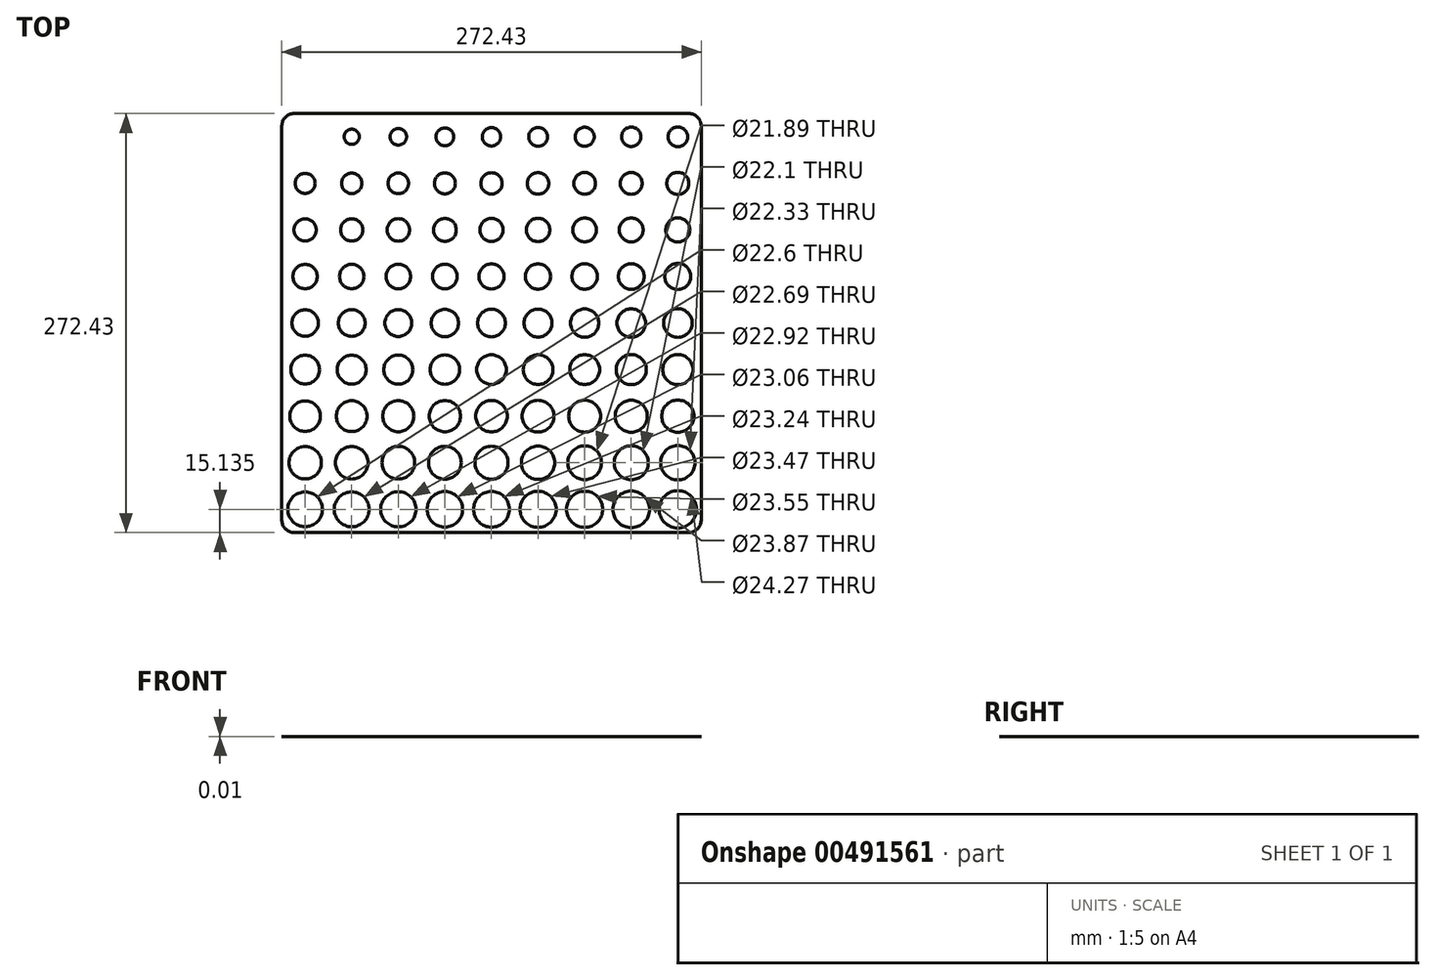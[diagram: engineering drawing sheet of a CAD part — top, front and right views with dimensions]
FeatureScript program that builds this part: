
annotation { "Feature Type Name" : "Feature", "Feature Type Description" : "" }
export const myFeature = defineFeature(function(context is Context, id is Id, definition is map)
    precondition{}
    {
        {
            var Q0;
            Q0=qCreatedBy(makeId("Top.planeOp"),FACE);
            var sketch = newSketch(context, id + "F0", { "sketchPlane" : qUnion([Q0])});
            skLineSegment(sketch, "E0.bottom", {"start": v(0, 0) * mm, "end": v(30.27, 0) * mm, "construction": true});
            skLineSegment(sketch, "E0.top", {"start": v(0, -30.27) * mm, "end": v(30.27, -30.27) * mm, "construction": true});
            skLineSegment(sketch, "E0.left", {"start": v(0, 0) * mm, "end": v(0, -30.27) * mm, "construction": true});
            skLineSegment(sketch, "E0.right", {"start": v(30.27, 0) * mm, "end": v(30.27, -30.27) * mm, "construction": true});
            skLineSegment(sketch, "E1", {"start": v(0, -15.13) * mm, "end": v(30.27, -15.13) * mm, "construction": true});
            skLineSegment(sketch, "E2", {"start": v(15.14, 0) * mm, "end": v(15.14, -30.27) * mm, "construction": true});
            skPoint(sketch, "E3", {"position": v(15.14, -15.14) * mm});
            skLineSegment(sketch, "E4.0.1.0", {"start": v(0, -30.27) * mm, "end": v(0, -60.54) * mm, "construction": true});
            skLineSegment(sketch, "E4.0.1.1", {"start": v(15.14, -30.27) * mm, "end": v(15.14, -60.54) * mm, "construction": true});
            skLineSegment(sketch, "E4.0.1.2", {"start": v(30.27, -30.27) * mm, "end": v(30.27, -60.54) * mm, "construction": true});
            skLineSegment(sketch, "E4.0.1.4", {"start": v(0, -60.54) * mm, "end": v(30.27, -60.54) * mm, "construction": true});
            skPoint(sketch, "E4.0.1.5", {"position": v(15.14, -45.4) * mm});
            skLineSegment(sketch, "E4.0.2.0", {"start": v(0, -60.54) * mm, "end": v(0, -90.81) * mm, "construction": true});
            skLineSegment(sketch, "E4.0.2.1", {"start": v(15.14, -60.54) * mm, "end": v(15.14, -90.81) * mm, "construction": true});
            skLineSegment(sketch, "E4.0.2.2", {"start": v(30.27, -60.54) * mm, "end": v(30.27, -90.81) * mm, "construction": true});
            skLineSegment(sketch, "E4.0.2.3", {"start": v(0, -60.54) * mm, "end": v(30.27, -60.54) * mm, "construction": true});
            skLineSegment(sketch, "E4.0.2.4", {"start": v(0, -90.81) * mm, "end": v(30.27, -90.81) * mm, "construction": true});
            skPoint(sketch, "E4.0.2.5", {"position": v(15.14, -75.68) * mm});
            skLineSegment(sketch, "E4.0.3.0", {"start": v(0, -90.81) * mm, "end": v(0, -121.08) * mm, "construction": true});
            skLineSegment(sketch, "E4.0.3.1", {"start": v(15.14, -90.81) * mm, "end": v(15.14, -121.08) * mm, "construction": true});
            skLineSegment(sketch, "E4.0.3.2", {"start": v(30.27, -90.81) * mm, "end": v(30.27, -121.08) * mm, "construction": true});
            skLineSegment(sketch, "E4.0.3.3", {"start": v(0, -90.81) * mm, "end": v(30.27, -90.81) * mm, "construction": true});
            skLineSegment(sketch, "E4.0.3.4", {"start": v(0, -121.08) * mm, "end": v(30.27, -121.08) * mm, "construction": true});
            skPoint(sketch, "E4.0.3.5", {"position": v(15.14, -105.94) * mm});
            skLineSegment(sketch, "E4.0.4.0", {"start": v(0, -121.08) * mm, "end": v(0, -151.35) * mm, "construction": true});
            skLineSegment(sketch, "E4.0.4.1", {"start": v(15.14, -121.08) * mm, "end": v(15.14, -151.35) * mm, "construction": true});
            skLineSegment(sketch, "E4.0.4.2", {"start": v(30.27, -121.08) * mm, "end": v(30.27, -151.35) * mm, "construction": true});
            skLineSegment(sketch, "E4.0.4.3", {"start": v(0, -121.08) * mm, "end": v(30.27, -121.08) * mm, "construction": true});
            skLineSegment(sketch, "E4.0.4.4", {"start": v(0, -151.35) * mm, "end": v(30.27, -151.35) * mm, "construction": true});
            skPoint(sketch, "E4.0.4.5", {"position": v(15.14, -136.22) * mm});
            skLineSegment(sketch, "E4.0.5.0", {"start": v(0, -151.35) * mm, "end": v(0, -181.62) * mm, "construction": true});
            skLineSegment(sketch, "E4.0.5.1", {"start": v(15.14, -151.35) * mm, "end": v(15.14, -181.62) * mm, "construction": true});
            skLineSegment(sketch, "E4.0.5.2", {"start": v(30.27, -151.35) * mm, "end": v(30.27, -181.62) * mm, "construction": true});
            skLineSegment(sketch, "E4.0.5.3", {"start": v(0, -151.35) * mm, "end": v(30.27, -151.35) * mm, "construction": true});
            skLineSegment(sketch, "E4.0.5.4", {"start": v(0, -181.62) * mm, "end": v(30.27, -181.62) * mm, "construction": true});
            skPoint(sketch, "E4.0.5.5", {"position": v(15.14, -166.49) * mm});
            skLineSegment(sketch, "E4.0.6.0", {"start": v(0, -181.62) * mm, "end": v(0, -211.89) * mm, "construction": true});
            skLineSegment(sketch, "E4.0.6.1", {"start": v(15.14, -181.62) * mm, "end": v(15.14, -211.9) * mm, "construction": true});
            skLineSegment(sketch, "E4.0.6.2", {"start": v(30.27, -181.62) * mm, "end": v(30.27, -211.89) * mm, "construction": true});
            skLineSegment(sketch, "E4.0.6.3", {"start": v(0, -181.62) * mm, "end": v(30.27, -181.62) * mm, "construction": true});
            skLineSegment(sketch, "E4.0.6.4", {"start": v(0, -211.89) * mm, "end": v(30.27, -211.89) * mm, "construction": true});
            skPoint(sketch, "E4.0.6.5", {"position": v(15.14, -196.76) * mm});
            skLineSegment(sketch, "E4.0.7.0", {"start": v(0, -211.9) * mm, "end": v(0, -242.16) * mm, "construction": true});
            skLineSegment(sketch, "E4.0.7.1", {"start": v(15.14, -211.9) * mm, "end": v(15.14, -242.16) * mm, "construction": true});
            skLineSegment(sketch, "E4.0.7.2", {"start": v(30.27, -211.9) * mm, "end": v(30.27, -242.16) * mm, "construction": true});
            skLineSegment(sketch, "E4.0.7.3", {"start": v(0, -211.9) * mm, "end": v(30.27, -211.9) * mm, "construction": true});
            skLineSegment(sketch, "E4.0.7.4", {"start": v(0, -242.16) * mm, "end": v(30.27, -242.16) * mm, "construction": true});
            skPoint(sketch, "E4.0.7.5", {"position": v(15.14, -227.03) * mm});
            skLineSegment(sketch, "E4.0.8.0", {"start": v(0, -242.16) * mm, "end": v(0, -272.43) * mm, "construction": true});
            skLineSegment(sketch, "E4.0.8.1", {"start": v(15.14, -242.16) * mm, "end": v(15.14, -272.43) * mm, "construction": true});
            skLineSegment(sketch, "E4.0.8.2", {"start": v(30.27, -242.16) * mm, "end": v(30.27, -272.43) * mm, "construction": true});
            skLineSegment(sketch, "E4.0.8.3", {"start": v(0, -242.16) * mm, "end": v(30.27, -242.16) * mm, "construction": true});
            skLineSegment(sketch, "E4.0.8.4", {"start": v(0, -272.43) * mm, "end": v(30.27, -272.43) * mm, "construction": true});
            skPoint(sketch, "E4.0.8.5", {"position": v(15.14, -257.3) * mm});
            skLineSegment(sketch, "E4.1.0.1", {"start": v(45.4, 0) * mm, "end": v(45.4, -30.27) * mm, "construction": true});
            skLineSegment(sketch, "E4.1.0.2", {"start": v(60.54, 0) * mm, "end": v(60.54, -30.27) * mm, "construction": true});
            skLineSegment(sketch, "E4.1.0.3", {"start": v(30.27, 0) * mm, "end": v(60.54, 0) * mm, "construction": true});
            skLineSegment(sketch, "E4.1.0.4", {"start": v(30.27, -30.27) * mm, "end": v(60.54, -30.27) * mm, "construction": true});
            skPoint(sketch, "E4.1.0.5", {"position": v(45.4, -15.14) * mm});
            skLineSegment(sketch, "E4.1.1.0", {"start": v(30.27, -30.27) * mm, "end": v(30.27, -60.54) * mm, "construction": true});
            skLineSegment(sketch, "E4.1.1.1", {"start": v(45.4, -30.27) * mm, "end": v(45.4, -60.54) * mm, "construction": true});
            skLineSegment(sketch, "E4.1.1.2", {"start": v(60.54, -30.27) * mm, "end": v(60.54, -60.54) * mm, "construction": true});
            skLineSegment(sketch, "E4.1.1.3", {"start": v(30.27, -30.27) * mm, "end": v(60.54, -30.27) * mm, "construction": true});
            skLineSegment(sketch, "E4.1.1.4", {"start": v(30.27, -60.54) * mm, "end": v(60.54, -60.54) * mm, "construction": true});
            skPoint(sketch, "E4.1.1.5", {"position": v(45.4, -45.4) * mm});
            skLineSegment(sketch, "E4.1.2.0", {"start": v(30.27, -60.54) * mm, "end": v(30.27, -90.81) * mm, "construction": true});
            skLineSegment(sketch, "E4.1.2.1", {"start": v(45.4, -60.54) * mm, "end": v(45.4, -90.81) * mm, "construction": true});
            skLineSegment(sketch, "E4.1.2.2", {"start": v(60.54, -60.54) * mm, "end": v(60.54, -90.81) * mm, "construction": true});
            skLineSegment(sketch, "E4.1.2.3", {"start": v(30.27, -60.54) * mm, "end": v(60.54, -60.54) * mm, "construction": true});
            skLineSegment(sketch, "E4.1.2.4", {"start": v(30.27, -90.81) * mm, "end": v(60.54, -90.81) * mm, "construction": true});
            skPoint(sketch, "E4.1.2.5", {"position": v(45.4, -75.68) * mm});
            skLineSegment(sketch, "E4.1.3.0", {"start": v(30.27, -90.81) * mm, "end": v(30.27, -121.08) * mm, "construction": true});
            skLineSegment(sketch, "E4.1.3.1", {"start": v(45.4, -90.81) * mm, "end": v(45.4, -121.08) * mm, "construction": true});
            skLineSegment(sketch, "E4.1.3.2", {"start": v(60.54, -90.81) * mm, "end": v(60.54, -121.08) * mm, "construction": true});
            skLineSegment(sketch, "E4.1.3.3", {"start": v(30.27, -90.81) * mm, "end": v(60.54, -90.81) * mm, "construction": true});
            skLineSegment(sketch, "E4.1.3.4", {"start": v(30.27, -121.08) * mm, "end": v(60.54, -121.08) * mm, "construction": true});
            skPoint(sketch, "E4.1.3.5", {"position": v(45.4, -105.94) * mm});
            skLineSegment(sketch, "E4.1.4.0", {"start": v(30.27, -121.08) * mm, "end": v(30.27, -151.35) * mm, "construction": true});
            skLineSegment(sketch, "E4.1.4.1", {"start": v(45.4, -121.08) * mm, "end": v(45.4, -151.35) * mm, "construction": true});
            skLineSegment(sketch, "E4.1.4.2", {"start": v(60.54, -121.08) * mm, "end": v(60.54, -151.35) * mm, "construction": true});
            skLineSegment(sketch, "E4.1.4.3", {"start": v(30.27, -121.08) * mm, "end": v(60.54, -121.08) * mm, "construction": true});
            skLineSegment(sketch, "E4.1.4.4", {"start": v(30.27, -151.35) * mm, "end": v(60.54, -151.35) * mm, "construction": true});
            skPoint(sketch, "E4.1.4.5", {"position": v(45.4, -136.22) * mm});
            skLineSegment(sketch, "E4.1.5.0", {"start": v(30.27, -151.35) * mm, "end": v(30.27, -181.62) * mm, "construction": true});
            skLineSegment(sketch, "E4.1.5.1", {"start": v(45.4, -151.35) * mm, "end": v(45.4, -181.62) * mm, "construction": true});
            skLineSegment(sketch, "E4.1.5.2", {"start": v(60.54, -151.35) * mm, "end": v(60.54, -181.62) * mm, "construction": true});
            skLineSegment(sketch, "E4.1.5.3", {"start": v(30.27, -151.35) * mm, "end": v(60.54, -151.35) * mm, "construction": true});
            skLineSegment(sketch, "E4.1.5.4", {"start": v(30.27, -181.62) * mm, "end": v(60.54, -181.62) * mm, "construction": true});
            skPoint(sketch, "E4.1.5.5", {"position": v(45.4, -166.49) * mm});
            skLineSegment(sketch, "E4.1.6.0", {"start": v(30.27, -181.62) * mm, "end": v(30.27, -211.89) * mm, "construction": true});
            skLineSegment(sketch, "E4.1.6.1", {"start": v(45.4, -181.62) * mm, "end": v(45.4, -211.9) * mm, "construction": true});
            skLineSegment(sketch, "E4.1.6.2", {"start": v(60.54, -181.62) * mm, "end": v(60.54, -211.89) * mm, "construction": true});
            skLineSegment(sketch, "E4.1.6.3", {"start": v(30.27, -181.62) * mm, "end": v(60.54, -181.62) * mm, "construction": true});
            skLineSegment(sketch, "E4.1.6.4", {"start": v(30.27, -211.89) * mm, "end": v(60.54, -211.89) * mm, "construction": true});
            skPoint(sketch, "E4.1.6.5", {"position": v(45.4, -196.76) * mm});
            skLineSegment(sketch, "E4.1.7.0", {"start": v(30.27, -211.9) * mm, "end": v(30.27, -242.16) * mm, "construction": true});
            skLineSegment(sketch, "E4.1.7.1", {"start": v(45.4, -211.9) * mm, "end": v(45.4, -242.16) * mm, "construction": true});
            skLineSegment(sketch, "E4.1.7.2", {"start": v(60.54, -211.9) * mm, "end": v(60.54, -242.16) * mm, "construction": true});
            skLineSegment(sketch, "E4.1.7.3", {"start": v(30.27, -211.9) * mm, "end": v(60.54, -211.9) * mm, "construction": true});
            skLineSegment(sketch, "E4.1.7.4", {"start": v(30.27, -242.16) * mm, "end": v(60.54, -242.16) * mm, "construction": true});
            skPoint(sketch, "E4.1.7.5", {"position": v(45.4, -227.03) * mm});
            skLineSegment(sketch, "E4.1.8.0", {"start": v(30.27, -242.16) * mm, "end": v(30.27, -272.43) * mm, "construction": true});
            skLineSegment(sketch, "E4.1.8.1", {"start": v(45.4, -242.16) * mm, "end": v(45.4, -272.43) * mm, "construction": true});
            skLineSegment(sketch, "E4.1.8.2", {"start": v(60.54, -242.16) * mm, "end": v(60.54, -272.43) * mm, "construction": true});
            skLineSegment(sketch, "E4.1.8.3", {"start": v(30.27, -242.16) * mm, "end": v(60.54, -242.16) * mm, "construction": true});
            skLineSegment(sketch, "E4.1.8.4", {"start": v(30.27, -272.43) * mm, "end": v(60.54, -272.43) * mm, "construction": true});
            skPoint(sketch, "E4.1.8.5", {"position": v(45.4, -257.3) * mm});
            skLineSegment(sketch, "E4.2.0.0", {"start": v(60.54, 0) * mm, "end": v(60.54, -30.27) * mm, "construction": true});
            skLineSegment(sketch, "E4.2.0.1", {"start": v(75.68, 0) * mm, "end": v(75.68, -30.27) * mm, "construction": true});
            skLineSegment(sketch, "E4.2.0.2", {"start": v(90.81, 0) * mm, "end": v(90.81, -30.27) * mm, "construction": true});
            skLineSegment(sketch, "E4.2.0.3", {"start": v(60.54, 0) * mm, "end": v(90.81, 0) * mm, "construction": true});
            skLineSegment(sketch, "E4.2.0.4", {"start": v(60.54, -30.27) * mm, "end": v(90.81, -30.27) * mm, "construction": true});
            skPoint(sketch, "E4.2.0.5", {"position": v(75.68, -15.14) * mm});
            skLineSegment(sketch, "E4.2.1.0", {"start": v(60.54, -30.27) * mm, "end": v(60.54, -60.54) * mm, "construction": true});
            skLineSegment(sketch, "E4.2.1.1", {"start": v(75.68, -30.27) * mm, "end": v(75.68, -60.54) * mm, "construction": true});
            skLineSegment(sketch, "E4.2.1.2", {"start": v(90.81, -30.27) * mm, "end": v(90.81, -60.54) * mm, "construction": true});
            skLineSegment(sketch, "E4.2.1.3", {"start": v(60.54, -30.27) * mm, "end": v(90.81, -30.27) * mm, "construction": true});
            skLineSegment(sketch, "E4.2.1.4", {"start": v(60.54, -60.54) * mm, "end": v(90.81, -60.54) * mm, "construction": true});
            skPoint(sketch, "E4.2.1.5", {"position": v(75.68, -45.4) * mm});
            skLineSegment(sketch, "E4.2.2.0", {"start": v(60.54, -60.54) * mm, "end": v(60.54, -90.81) * mm, "construction": true});
            skLineSegment(sketch, "E4.2.2.1", {"start": v(75.68, -60.54) * mm, "end": v(75.68, -90.81) * mm, "construction": true});
            skLineSegment(sketch, "E4.2.2.2", {"start": v(90.81, -60.54) * mm, "end": v(90.81, -90.81) * mm, "construction": true});
            skLineSegment(sketch, "E4.2.2.3", {"start": v(60.54, -60.54) * mm, "end": v(90.81, -60.54) * mm, "construction": true});
            skLineSegment(sketch, "E4.2.2.4", {"start": v(60.54, -90.81) * mm, "end": v(90.81, -90.81) * mm, "construction": true});
            skPoint(sketch, "E4.2.2.5", {"position": v(75.68, -75.68) * mm});
            skLineSegment(sketch, "E4.2.3.0", {"start": v(60.54, -90.81) * mm, "end": v(60.54, -121.08) * mm, "construction": true});
            skLineSegment(sketch, "E4.2.3.1", {"start": v(75.68, -90.81) * mm, "end": v(75.68, -121.08) * mm, "construction": true});
            skLineSegment(sketch, "E4.2.3.2", {"start": v(90.81, -90.81) * mm, "end": v(90.81, -121.08) * mm, "construction": true});
            skLineSegment(sketch, "E4.2.3.3", {"start": v(60.54, -90.81) * mm, "end": v(90.81, -90.81) * mm, "construction": true});
            skLineSegment(sketch, "E4.2.3.4", {"start": v(60.54, -121.08) * mm, "end": v(90.81, -121.08) * mm, "construction": true});
            skPoint(sketch, "E4.2.3.5", {"position": v(75.68, -105.94) * mm});
            skLineSegment(sketch, "E4.2.4.0", {"start": v(60.54, -121.08) * mm, "end": v(60.54, -151.35) * mm, "construction": true});
            skLineSegment(sketch, "E4.2.4.1", {"start": v(75.68, -121.08) * mm, "end": v(75.68, -151.35) * mm, "construction": true});
            skLineSegment(sketch, "E4.2.4.2", {"start": v(90.81, -121.08) * mm, "end": v(90.81, -151.35) * mm, "construction": true});
            skLineSegment(sketch, "E4.2.4.3", {"start": v(60.54, -121.08) * mm, "end": v(90.81, -121.08) * mm, "construction": true});
            skLineSegment(sketch, "E4.2.4.4", {"start": v(60.54, -151.35) * mm, "end": v(90.81, -151.35) * mm, "construction": true});
            skPoint(sketch, "E4.2.4.5", {"position": v(75.68, -136.22) * mm});
            skLineSegment(sketch, "E4.2.5.0", {"start": v(60.54, -151.35) * mm, "end": v(60.54, -181.62) * mm, "construction": true});
            skLineSegment(sketch, "E4.2.5.1", {"start": v(75.68, -151.35) * mm, "end": v(75.68, -181.62) * mm, "construction": true});
            skLineSegment(sketch, "E4.2.5.2", {"start": v(90.81, -151.35) * mm, "end": v(90.81, -181.62) * mm, "construction": true});
            skLineSegment(sketch, "E4.2.5.3", {"start": v(60.54, -151.35) * mm, "end": v(90.81, -151.35) * mm, "construction": true});
            skLineSegment(sketch, "E4.2.5.4", {"start": v(60.54, -181.62) * mm, "end": v(90.81, -181.62) * mm, "construction": true});
            skPoint(sketch, "E4.2.5.5", {"position": v(75.68, -166.49) * mm});
            skLineSegment(sketch, "E4.2.6.0", {"start": v(60.54, -181.62) * mm, "end": v(60.54, -211.89) * mm, "construction": true});
            skLineSegment(sketch, "E4.2.6.1", {"start": v(75.68, -181.62) * mm, "end": v(75.68, -211.9) * mm, "construction": true});
            skLineSegment(sketch, "E4.2.6.2", {"start": v(90.81, -181.62) * mm, "end": v(90.81, -211.89) * mm, "construction": true});
            skLineSegment(sketch, "E4.2.6.3", {"start": v(60.54, -181.62) * mm, "end": v(90.81, -181.62) * mm, "construction": true});
            skLineSegment(sketch, "E4.2.6.4", {"start": v(60.54, -211.89) * mm, "end": v(90.81, -211.89) * mm, "construction": true});
            skPoint(sketch, "E4.2.6.5", {"position": v(75.68, -196.76) * mm});
            skLineSegment(sketch, "E4.2.7.0", {"start": v(60.54, -211.9) * mm, "end": v(60.54, -242.16) * mm, "construction": true});
            skLineSegment(sketch, "E4.2.7.1", {"start": v(75.68, -211.9) * mm, "end": v(75.68, -242.16) * mm, "construction": true});
            skLineSegment(sketch, "E4.2.7.2", {"start": v(90.81, -211.9) * mm, "end": v(90.81, -242.16) * mm, "construction": true});
            skLineSegment(sketch, "E4.2.7.3", {"start": v(60.54, -211.9) * mm, "end": v(90.81, -211.9) * mm, "construction": true});
            skLineSegment(sketch, "E4.2.7.4", {"start": v(60.54, -242.16) * mm, "end": v(90.81, -242.16) * mm, "construction": true});
            skPoint(sketch, "E4.2.7.5", {"position": v(75.68, -227.03) * mm});
            skLineSegment(sketch, "E4.2.8.0", {"start": v(60.54, -242.16) * mm, "end": v(60.54, -272.43) * mm, "construction": true});
            skLineSegment(sketch, "E4.2.8.1", {"start": v(75.68, -242.16) * mm, "end": v(75.68, -272.43) * mm, "construction": true});
            skLineSegment(sketch, "E4.2.8.2", {"start": v(90.81, -242.16) * mm, "end": v(90.81, -272.43) * mm, "construction": true});
            skLineSegment(sketch, "E4.2.8.3", {"start": v(60.54, -242.16) * mm, "end": v(90.81, -242.16) * mm, "construction": true});
            skLineSegment(sketch, "E4.2.8.4", {"start": v(60.54, -272.43) * mm, "end": v(90.81, -272.43) * mm, "construction": true});
            skPoint(sketch, "E4.2.8.5", {"position": v(75.68, -257.3) * mm});
            skLineSegment(sketch, "E4.3.0.0", {"start": v(90.81, 0) * mm, "end": v(90.81, -30.27) * mm, "construction": true});
            skLineSegment(sketch, "E4.3.0.1", {"start": v(105.95, 0) * mm, "end": v(105.95, -30.27) * mm, "construction": true});
            skLineSegment(sketch, "E4.3.0.2", {"start": v(121.08, 0) * mm, "end": v(121.08, -30.27) * mm, "construction": true});
            skLineSegment(sketch, "E4.3.0.3", {"start": v(90.81, 0) * mm, "end": v(121.08, 0) * mm, "construction": true});
            skLineSegment(sketch, "E4.3.0.4", {"start": v(90.81, -30.27) * mm, "end": v(121.08, -30.27) * mm, "construction": true});
            skPoint(sketch, "E4.3.0.5", {"position": v(105.95, -15.14) * mm});
            skLineSegment(sketch, "E4.3.1.0", {"start": v(90.81, -30.27) * mm, "end": v(90.81, -60.54) * mm, "construction": true});
            skLineSegment(sketch, "E4.3.1.1", {"start": v(105.95, -30.27) * mm, "end": v(105.95, -60.54) * mm, "construction": true});
            skLineSegment(sketch, "E4.3.1.2", {"start": v(121.08, -30.27) * mm, "end": v(121.08, -60.54) * mm, "construction": true});
            skLineSegment(sketch, "E4.3.1.3", {"start": v(90.81, -30.27) * mm, "end": v(121.08, -30.27) * mm, "construction": true});
            skLineSegment(sketch, "E4.3.1.4", {"start": v(90.81, -60.54) * mm, "end": v(121.08, -60.54) * mm, "construction": true});
            skPoint(sketch, "E4.3.1.5", {"position": v(105.95, -45.4) * mm});
            skLineSegment(sketch, "E4.3.2.0", {"start": v(90.81, -60.54) * mm, "end": v(90.81, -90.81) * mm, "construction": true});
            skLineSegment(sketch, "E4.3.2.1", {"start": v(105.95, -60.54) * mm, "end": v(105.95, -90.81) * mm, "construction": true});
            skLineSegment(sketch, "E4.3.2.2", {"start": v(121.08, -60.54) * mm, "end": v(121.08, -90.81) * mm, "construction": true});
            skLineSegment(sketch, "E4.3.2.3", {"start": v(90.81, -60.54) * mm, "end": v(121.08, -60.54) * mm, "construction": true});
            skLineSegment(sketch, "E4.3.2.4", {"start": v(90.81, -90.81) * mm, "end": v(121.08, -90.81) * mm, "construction": true});
            skPoint(sketch, "E4.3.2.5", {"position": v(105.95, -75.68) * mm});
            skLineSegment(sketch, "E4.3.3.0", {"start": v(90.81, -90.81) * mm, "end": v(90.81, -121.08) * mm, "construction": true});
            skLineSegment(sketch, "E4.3.3.1", {"start": v(105.95, -90.81) * mm, "end": v(105.95, -121.08) * mm, "construction": true});
            skLineSegment(sketch, "E4.3.3.2", {"start": v(121.08, -90.81) * mm, "end": v(121.08, -121.08) * mm, "construction": true});
            skLineSegment(sketch, "E4.3.3.3", {"start": v(90.81, -90.81) * mm, "end": v(121.08, -90.81) * mm, "construction": true});
            skLineSegment(sketch, "E4.3.3.4", {"start": v(90.81, -121.08) * mm, "end": v(121.08, -121.08) * mm, "construction": true});
            skPoint(sketch, "E4.3.3.5", {"position": v(105.95, -105.94) * mm});
            skLineSegment(sketch, "E4.3.4.0", {"start": v(90.81, -121.08) * mm, "end": v(90.81, -151.35) * mm, "construction": true});
            skLineSegment(sketch, "E4.3.4.1", {"start": v(105.95, -121.08) * mm, "end": v(105.95, -151.35) * mm, "construction": true});
            skLineSegment(sketch, "E4.3.4.2", {"start": v(121.08, -121.08) * mm, "end": v(121.08, -151.35) * mm, "construction": true});
            skLineSegment(sketch, "E4.3.4.3", {"start": v(90.81, -121.08) * mm, "end": v(121.08, -121.08) * mm, "construction": true});
            skLineSegment(sketch, "E4.3.4.4", {"start": v(90.81, -151.35) * mm, "end": v(121.08, -151.35) * mm, "construction": true});
            skPoint(sketch, "E4.3.4.5", {"position": v(105.95, -136.22) * mm});
            skLineSegment(sketch, "E4.3.5.0", {"start": v(90.81, -151.35) * mm, "end": v(90.81, -181.62) * mm, "construction": true});
            skLineSegment(sketch, "E4.3.5.1", {"start": v(105.95, -151.35) * mm, "end": v(105.95, -181.62) * mm, "construction": true});
            skLineSegment(sketch, "E4.3.5.2", {"start": v(121.08, -151.35) * mm, "end": v(121.08, -181.62) * mm, "construction": true});
            skLineSegment(sketch, "E4.3.5.3", {"start": v(90.81, -151.35) * mm, "end": v(121.08, -151.35) * mm, "construction": true});
            skLineSegment(sketch, "E4.3.5.4", {"start": v(90.81, -181.62) * mm, "end": v(121.08, -181.62) * mm, "construction": true});
            skPoint(sketch, "E4.3.5.5", {"position": v(105.95, -166.49) * mm});
            skLineSegment(sketch, "E4.3.6.0", {"start": v(90.81, -181.62) * mm, "end": v(90.81, -211.89) * mm, "construction": true});
            skLineSegment(sketch, "E4.3.6.1", {"start": v(105.95, -181.62) * mm, "end": v(105.95, -211.9) * mm, "construction": true});
            skLineSegment(sketch, "E4.3.6.2", {"start": v(121.08, -181.62) * mm, "end": v(121.08, -211.89) * mm, "construction": true});
            skLineSegment(sketch, "E4.3.6.3", {"start": v(90.81, -181.62) * mm, "end": v(121.08, -181.62) * mm, "construction": true});
            skLineSegment(sketch, "E4.3.6.4", {"start": v(90.81, -211.89) * mm, "end": v(121.08, -211.89) * mm, "construction": true});
            skPoint(sketch, "E4.3.6.5", {"position": v(105.95, -196.76) * mm});
            skLineSegment(sketch, "E4.3.7.0", {"start": v(90.81, -211.9) * mm, "end": v(90.81, -242.16) * mm, "construction": true});
            skLineSegment(sketch, "E4.3.7.1", {"start": v(105.95, -211.9) * mm, "end": v(105.95, -242.16) * mm, "construction": true});
            skLineSegment(sketch, "E4.3.7.2", {"start": v(121.08, -211.9) * mm, "end": v(121.08, -242.16) * mm, "construction": true});
            skLineSegment(sketch, "E4.3.7.3", {"start": v(90.81, -211.9) * mm, "end": v(121.08, -211.9) * mm, "construction": true});
            skLineSegment(sketch, "E4.3.7.4", {"start": v(90.81, -242.16) * mm, "end": v(121.08, -242.16) * mm, "construction": true});
            skPoint(sketch, "E4.3.7.5", {"position": v(105.95, -227.03) * mm});
            skLineSegment(sketch, "E4.3.8.0", {"start": v(90.81, -242.16) * mm, "end": v(90.81, -272.43) * mm, "construction": true});
            skLineSegment(sketch, "E4.3.8.1", {"start": v(105.95, -242.16) * mm, "end": v(105.95, -272.43) * mm, "construction": true});
            skLineSegment(sketch, "E4.3.8.2", {"start": v(121.08, -242.16) * mm, "end": v(121.08, -272.43) * mm, "construction": true});
            skLineSegment(sketch, "E4.3.8.3", {"start": v(90.81, -242.16) * mm, "end": v(121.08, -242.16) * mm, "construction": true});
            skLineSegment(sketch, "E4.3.8.4", {"start": v(90.81, -272.43) * mm, "end": v(121.08, -272.43) * mm, "construction": true});
            skPoint(sketch, "E4.3.8.5", {"position": v(105.95, -257.3) * mm});
            skLineSegment(sketch, "E4.4.0.0", {"start": v(121.08, 0) * mm, "end": v(121.08, -30.27) * mm, "construction": true});
            skLineSegment(sketch, "E4.4.0.1", {"start": v(136.22, 0) * mm, "end": v(136.22, -30.27) * mm, "construction": true});
            skLineSegment(sketch, "E4.4.0.2", {"start": v(151.35, 0) * mm, "end": v(151.35, -30.27) * mm, "construction": true});
            skLineSegment(sketch, "E4.4.0.3", {"start": v(121.08, 0) * mm, "end": v(151.35, 0) * mm, "construction": true});
            skLineSegment(sketch, "E4.4.0.4", {"start": v(121.08, -30.27) * mm, "end": v(151.35, -30.27) * mm, "construction": true});
            skPoint(sketch, "E4.4.0.5", {"position": v(136.22, -15.14) * mm});
            skLineSegment(sketch, "E4.4.1.0", {"start": v(121.08, -30.27) * mm, "end": v(121.08, -60.54) * mm, "construction": true});
            skLineSegment(sketch, "E4.4.1.1", {"start": v(136.22, -30.27) * mm, "end": v(136.22, -60.54) * mm, "construction": true});
            skLineSegment(sketch, "E4.4.1.2", {"start": v(151.35, -30.27) * mm, "end": v(151.35, -60.54) * mm, "construction": true});
            skLineSegment(sketch, "E4.4.1.3", {"start": v(121.08, -30.27) * mm, "end": v(151.35, -30.27) * mm, "construction": true});
            skLineSegment(sketch, "E4.4.1.4", {"start": v(121.08, -60.54) * mm, "end": v(151.35, -60.54) * mm, "construction": true});
            skPoint(sketch, "E4.4.1.5", {"position": v(136.22, -45.4) * mm});
            skLineSegment(sketch, "E4.4.2.0", {"start": v(121.08, -60.54) * mm, "end": v(121.08, -90.81) * mm, "construction": true});
            skLineSegment(sketch, "E4.4.2.1", {"start": v(136.22, -60.54) * mm, "end": v(136.22, -90.81) * mm, "construction": true});
            skLineSegment(sketch, "E4.4.2.2", {"start": v(151.35, -60.54) * mm, "end": v(151.35, -90.81) * mm, "construction": true});
            skLineSegment(sketch, "E4.4.2.3", {"start": v(121.08, -60.54) * mm, "end": v(151.35, -60.54) * mm, "construction": true});
            skLineSegment(sketch, "E4.4.2.4", {"start": v(121.08, -90.81) * mm, "end": v(151.35, -90.81) * mm, "construction": true});
            skPoint(sketch, "E4.4.2.5", {"position": v(136.22, -75.68) * mm});
            skLineSegment(sketch, "E4.4.3.0", {"start": v(121.08, -90.81) * mm, "end": v(121.08, -121.08) * mm, "construction": true});
            skLineSegment(sketch, "E4.4.3.1", {"start": v(136.22, -90.81) * mm, "end": v(136.22, -121.08) * mm, "construction": true});
            skLineSegment(sketch, "E4.4.3.2", {"start": v(151.35, -90.81) * mm, "end": v(151.35, -121.08) * mm, "construction": true});
            skLineSegment(sketch, "E4.4.3.3", {"start": v(121.08, -90.81) * mm, "end": v(151.35, -90.81) * mm, "construction": true});
            skLineSegment(sketch, "E4.4.3.4", {"start": v(121.08, -121.08) * mm, "end": v(151.35, -121.08) * mm, "construction": true});
            skPoint(sketch, "E4.4.3.5", {"position": v(136.22, -105.94) * mm});
            skLineSegment(sketch, "E4.4.4.0", {"start": v(121.08, -121.08) * mm, "end": v(121.08, -151.35) * mm, "construction": true});
            skLineSegment(sketch, "E4.4.4.1", {"start": v(136.22, -121.08) * mm, "end": v(136.22, -151.35) * mm, "construction": true});
            skLineSegment(sketch, "E4.4.4.2", {"start": v(151.35, -121.08) * mm, "end": v(151.35, -151.35) * mm, "construction": true});
            skLineSegment(sketch, "E4.4.4.3", {"start": v(121.08, -121.08) * mm, "end": v(151.35, -121.08) * mm, "construction": true});
            skLineSegment(sketch, "E4.4.4.4", {"start": v(121.08, -151.35) * mm, "end": v(151.35, -151.35) * mm, "construction": true});
            skPoint(sketch, "E4.4.4.5", {"position": v(136.22, -136.22) * mm});
            skLineSegment(sketch, "E4.4.5.0", {"start": v(121.08, -151.35) * mm, "end": v(121.08, -181.62) * mm, "construction": true});
            skLineSegment(sketch, "E4.4.5.1", {"start": v(136.22, -151.35) * mm, "end": v(136.22, -181.62) * mm, "construction": true});
            skLineSegment(sketch, "E4.4.5.2", {"start": v(151.35, -151.35) * mm, "end": v(151.35, -181.62) * mm, "construction": true});
            skLineSegment(sketch, "E4.4.5.3", {"start": v(121.08, -151.35) * mm, "end": v(151.35, -151.35) * mm, "construction": true});
            skLineSegment(sketch, "E4.4.5.4", {"start": v(121.08, -181.62) * mm, "end": v(151.35, -181.62) * mm, "construction": true});
            skPoint(sketch, "E4.4.5.5", {"position": v(136.22, -166.49) * mm});
            skLineSegment(sketch, "E4.4.6.0", {"start": v(121.08, -181.62) * mm, "end": v(121.08, -211.89) * mm, "construction": true});
            skLineSegment(sketch, "E4.4.6.1", {"start": v(136.22, -181.62) * mm, "end": v(136.22, -211.9) * mm, "construction": true});
            skLineSegment(sketch, "E4.4.6.2", {"start": v(151.35, -181.62) * mm, "end": v(151.35, -211.89) * mm, "construction": true});
            skLineSegment(sketch, "E4.4.6.3", {"start": v(121.08, -181.62) * mm, "end": v(151.35, -181.62) * mm, "construction": true});
            skLineSegment(sketch, "E4.4.6.4", {"start": v(121.08, -211.89) * mm, "end": v(151.35, -211.89) * mm, "construction": true});
            skPoint(sketch, "E4.4.6.5", {"position": v(136.22, -196.76) * mm});
            skLineSegment(sketch, "E4.4.7.0", {"start": v(121.08, -211.9) * mm, "end": v(121.08, -242.16) * mm, "construction": true});
            skLineSegment(sketch, "E4.4.7.1", {"start": v(136.22, -211.9) * mm, "end": v(136.22, -242.16) * mm, "construction": true});
            skLineSegment(sketch, "E4.4.7.2", {"start": v(151.35, -211.9) * mm, "end": v(151.35, -242.16) * mm, "construction": true});
            skLineSegment(sketch, "E4.4.7.3", {"start": v(121.08, -211.9) * mm, "end": v(151.35, -211.9) * mm, "construction": true});
            skLineSegment(sketch, "E4.4.7.4", {"start": v(121.08, -242.16) * mm, "end": v(151.35, -242.16) * mm, "construction": true});
            skPoint(sketch, "E4.4.7.5", {"position": v(136.22, -227.03) * mm});
            skLineSegment(sketch, "E4.4.8.0", {"start": v(121.08, -242.16) * mm, "end": v(121.08, -272.43) * mm, "construction": true});
            skLineSegment(sketch, "E4.4.8.1", {"start": v(136.22, -242.16) * mm, "end": v(136.22, -272.43) * mm, "construction": true});
            skLineSegment(sketch, "E4.4.8.2", {"start": v(151.35, -242.16) * mm, "end": v(151.35, -272.43) * mm, "construction": true});
            skLineSegment(sketch, "E4.4.8.3", {"start": v(121.08, -242.16) * mm, "end": v(151.35, -242.16) * mm, "construction": true});
            skLineSegment(sketch, "E4.4.8.4", {"start": v(121.08, -272.43) * mm, "end": v(151.35, -272.43) * mm, "construction": true});
            skPoint(sketch, "E4.4.8.5", {"position": v(136.22, -257.3) * mm});
            skLineSegment(sketch, "E4.5.0.0", {"start": v(151.35, 0) * mm, "end": v(151.35, -30.27) * mm, "construction": true});
            skLineSegment(sketch, "E4.5.0.1", {"start": v(166.49, 0) * mm, "end": v(166.49, -30.27) * mm, "construction": true});
            skLineSegment(sketch, "E4.5.0.2", {"start": v(181.62, 0) * mm, "end": v(181.62, -30.27) * mm, "construction": true});
            skLineSegment(sketch, "E4.5.0.3", {"start": v(151.35, 0) * mm, "end": v(181.62, 0) * mm, "construction": true});
            skLineSegment(sketch, "E4.5.0.4", {"start": v(151.35, -30.27) * mm, "end": v(181.62, -30.27) * mm, "construction": true});
            skPoint(sketch, "E4.5.0.5", {"position": v(166.49, -15.14) * mm});
            skLineSegment(sketch, "E4.5.1.0", {"start": v(151.35, -30.27) * mm, "end": v(151.35, -60.54) * mm, "construction": true});
            skLineSegment(sketch, "E4.5.1.1", {"start": v(166.49, -30.27) * mm, "end": v(166.49, -60.54) * mm, "construction": true});
            skLineSegment(sketch, "E4.5.1.2", {"start": v(181.62, -30.27) * mm, "end": v(181.62, -60.54) * mm, "construction": true});
            skLineSegment(sketch, "E4.5.1.3", {"start": v(151.35, -30.27) * mm, "end": v(181.62, -30.27) * mm, "construction": true});
            skLineSegment(sketch, "E4.5.1.4", {"start": v(151.35, -60.54) * mm, "end": v(181.62, -60.54) * mm, "construction": true});
            skPoint(sketch, "E4.5.1.5", {"position": v(166.49, -45.4) * mm});
            skLineSegment(sketch, "E4.5.2.0", {"start": v(151.35, -60.54) * mm, "end": v(151.35, -90.81) * mm, "construction": true});
            skLineSegment(sketch, "E4.5.2.1", {"start": v(166.49, -60.54) * mm, "end": v(166.49, -90.81) * mm, "construction": true});
            skLineSegment(sketch, "E4.5.2.2", {"start": v(181.62, -60.54) * mm, "end": v(181.62, -90.81) * mm, "construction": true});
            skLineSegment(sketch, "E4.5.2.3", {"start": v(151.35, -60.54) * mm, "end": v(181.62, -60.54) * mm, "construction": true});
            skLineSegment(sketch, "E4.5.2.4", {"start": v(151.35, -90.81) * mm, "end": v(181.62, -90.81) * mm, "construction": true});
            skPoint(sketch, "E4.5.2.5", {"position": v(166.49, -75.68) * mm});
            skLineSegment(sketch, "E4.5.3.0", {"start": v(151.35, -90.81) * mm, "end": v(151.35, -121.08) * mm, "construction": true});
            skLineSegment(sketch, "E4.5.3.1", {"start": v(166.49, -90.81) * mm, "end": v(166.49, -121.08) * mm, "construction": true});
            skLineSegment(sketch, "E4.5.3.2", {"start": v(181.62, -90.81) * mm, "end": v(181.62, -121.08) * mm, "construction": true});
            skLineSegment(sketch, "E4.5.3.3", {"start": v(151.35, -90.81) * mm, "end": v(181.62, -90.81) * mm, "construction": true});
            skLineSegment(sketch, "E4.5.3.4", {"start": v(151.35, -121.08) * mm, "end": v(181.62, -121.08) * mm, "construction": true});
            skPoint(sketch, "E4.5.3.5", {"position": v(166.49, -105.94) * mm});
            skLineSegment(sketch, "E4.5.4.0", {"start": v(151.35, -121.08) * mm, "end": v(151.35, -151.35) * mm, "construction": true});
            skLineSegment(sketch, "E4.5.4.1", {"start": v(166.49, -121.08) * mm, "end": v(166.49, -151.35) * mm, "construction": true});
            skLineSegment(sketch, "E4.5.4.2", {"start": v(181.62, -121.08) * mm, "end": v(181.62, -151.35) * mm, "construction": true});
            skLineSegment(sketch, "E4.5.4.3", {"start": v(151.35, -121.08) * mm, "end": v(181.62, -121.08) * mm, "construction": true});
            skLineSegment(sketch, "E4.5.4.4", {"start": v(151.35, -151.35) * mm, "end": v(181.62, -151.35) * mm, "construction": true});
            skPoint(sketch, "E4.5.4.5", {"position": v(166.49, -136.22) * mm});
            skLineSegment(sketch, "E4.5.5.0", {"start": v(151.35, -151.35) * mm, "end": v(151.35, -181.62) * mm, "construction": true});
            skLineSegment(sketch, "E4.5.5.1", {"start": v(166.49, -151.35) * mm, "end": v(166.49, -181.62) * mm, "construction": true});
            skLineSegment(sketch, "E4.5.5.2", {"start": v(181.62, -151.35) * mm, "end": v(181.62, -181.62) * mm, "construction": true});
            skLineSegment(sketch, "E4.5.5.3", {"start": v(151.35, -151.35) * mm, "end": v(181.62, -151.35) * mm, "construction": true});
            skLineSegment(sketch, "E4.5.5.4", {"start": v(151.35, -181.62) * mm, "end": v(181.62, -181.62) * mm, "construction": true});
            skPoint(sketch, "E4.5.5.5", {"position": v(166.49, -166.49) * mm});
            skLineSegment(sketch, "E4.5.6.0", {"start": v(151.35, -181.62) * mm, "end": v(151.35, -211.89) * mm, "construction": true});
            skLineSegment(sketch, "E4.5.6.1", {"start": v(166.49, -181.62) * mm, "end": v(166.49, -211.9) * mm, "construction": true});
            skLineSegment(sketch, "E4.5.6.2", {"start": v(181.62, -181.62) * mm, "end": v(181.62, -211.89) * mm, "construction": true});
            skLineSegment(sketch, "E4.5.6.3", {"start": v(151.35, -181.62) * mm, "end": v(181.62, -181.62) * mm, "construction": true});
            skLineSegment(sketch, "E4.5.6.4", {"start": v(151.35, -211.89) * mm, "end": v(181.62, -211.89) * mm, "construction": true});
            skPoint(sketch, "E4.5.6.5", {"position": v(166.49, -196.76) * mm});
            skLineSegment(sketch, "E4.5.7.0", {"start": v(151.35, -211.9) * mm, "end": v(151.35, -242.16) * mm, "construction": true});
            skLineSegment(sketch, "E4.5.7.1", {"start": v(166.49, -211.9) * mm, "end": v(166.49, -242.16) * mm, "construction": true});
            skLineSegment(sketch, "E4.5.7.2", {"start": v(181.62, -211.9) * mm, "end": v(181.62, -242.16) * mm, "construction": true});
            skLineSegment(sketch, "E4.5.7.3", {"start": v(151.35, -211.9) * mm, "end": v(181.62, -211.9) * mm, "construction": true});
            skLineSegment(sketch, "E4.5.7.4", {"start": v(151.35, -242.16) * mm, "end": v(181.62, -242.16) * mm, "construction": true});
            skPoint(sketch, "E4.5.7.5", {"position": v(166.49, -227.03) * mm});
            skLineSegment(sketch, "E4.5.8.0", {"start": v(151.35, -242.16) * mm, "end": v(151.35, -272.43) * mm, "construction": true});
            skLineSegment(sketch, "E4.5.8.1", {"start": v(166.49, -242.16) * mm, "end": v(166.49, -272.43) * mm, "construction": true});
            skLineSegment(sketch, "E4.5.8.2", {"start": v(181.62, -242.16) * mm, "end": v(181.62, -272.43) * mm, "construction": true});
            skLineSegment(sketch, "E4.5.8.3", {"start": v(151.35, -242.16) * mm, "end": v(181.62, -242.16) * mm, "construction": true});
            skLineSegment(sketch, "E4.5.8.4", {"start": v(151.35, -272.43) * mm, "end": v(181.62, -272.43) * mm, "construction": true});
            skPoint(sketch, "E4.5.8.5", {"position": v(166.49, -257.3) * mm});
            skLineSegment(sketch, "E4.6.0.0", {"start": v(181.62, 0) * mm, "end": v(181.62, -30.27) * mm, "construction": true});
            skLineSegment(sketch, "E4.6.0.1", {"start": v(196.76, 0) * mm, "end": v(196.76, -30.27) * mm, "construction": true});
            skLineSegment(sketch, "E4.6.0.2", {"start": v(211.89, 0) * mm, "end": v(211.89, -30.27) * mm, "construction": true});
            skLineSegment(sketch, "E4.6.0.3", {"start": v(181.62, 0) * mm, "end": v(211.89, 0) * mm, "construction": true});
            skLineSegment(sketch, "E4.6.0.4", {"start": v(181.62, -30.27) * mm, "end": v(211.89, -30.27) * mm, "construction": true});
            skPoint(sketch, "E4.6.0.5", {"position": v(196.76, -15.14) * mm});
            skLineSegment(sketch, "E4.6.1.0", {"start": v(181.62, -30.27) * mm, "end": v(181.62, -60.54) * mm, "construction": true});
            skLineSegment(sketch, "E4.6.1.1", {"start": v(196.76, -30.27) * mm, "end": v(196.76, -60.54) * mm, "construction": true});
            skLineSegment(sketch, "E4.6.1.2", {"start": v(211.89, -30.27) * mm, "end": v(211.89, -60.54) * mm, "construction": true});
            skLineSegment(sketch, "E4.6.1.3", {"start": v(181.62, -30.27) * mm, "end": v(211.89, -30.27) * mm, "construction": true});
            skLineSegment(sketch, "E4.6.1.4", {"start": v(181.62, -60.54) * mm, "end": v(211.89, -60.54) * mm, "construction": true});
            skPoint(sketch, "E4.6.1.5", {"position": v(196.76, -45.4) * mm});
            skLineSegment(sketch, "E4.6.2.0", {"start": v(181.62, -60.54) * mm, "end": v(181.62, -90.81) * mm, "construction": true});
            skLineSegment(sketch, "E4.6.2.1", {"start": v(196.76, -60.54) * mm, "end": v(196.76, -90.81) * mm, "construction": true});
            skLineSegment(sketch, "E4.6.2.2", {"start": v(211.89, -60.54) * mm, "end": v(211.89, -90.81) * mm, "construction": true});
            skLineSegment(sketch, "E4.6.2.3", {"start": v(181.62, -60.54) * mm, "end": v(211.89, -60.54) * mm, "construction": true});
            skLineSegment(sketch, "E4.6.2.4", {"start": v(181.62, -90.81) * mm, "end": v(211.89, -90.81) * mm, "construction": true});
            skPoint(sketch, "E4.6.2.5", {"position": v(196.76, -75.68) * mm});
            skLineSegment(sketch, "E4.6.3.0", {"start": v(181.62, -90.81) * mm, "end": v(181.62, -121.08) * mm, "construction": true});
            skLineSegment(sketch, "E4.6.3.1", {"start": v(196.76, -90.81) * mm, "end": v(196.76, -121.08) * mm, "construction": true});
            skLineSegment(sketch, "E4.6.3.2", {"start": v(211.89, -90.81) * mm, "end": v(211.89, -121.08) * mm, "construction": true});
            skLineSegment(sketch, "E4.6.3.3", {"start": v(181.62, -90.81) * mm, "end": v(211.89, -90.81) * mm, "construction": true});
            skLineSegment(sketch, "E4.6.3.4", {"start": v(181.62, -121.08) * mm, "end": v(211.89, -121.08) * mm, "construction": true});
            skPoint(sketch, "E4.6.3.5", {"position": v(196.76, -105.94) * mm});
            skLineSegment(sketch, "E4.6.4.0", {"start": v(181.62, -121.08) * mm, "end": v(181.62, -151.35) * mm, "construction": true});
            skLineSegment(sketch, "E4.6.4.1", {"start": v(196.76, -121.08) * mm, "end": v(196.76, -151.35) * mm, "construction": true});
            skLineSegment(sketch, "E4.6.4.2", {"start": v(211.89, -121.08) * mm, "end": v(211.89, -151.35) * mm, "construction": true});
            skLineSegment(sketch, "E4.6.4.3", {"start": v(181.62, -121.08) * mm, "end": v(211.89, -121.08) * mm, "construction": true});
            skLineSegment(sketch, "E4.6.4.4", {"start": v(181.62, -151.35) * mm, "end": v(211.89, -151.35) * mm, "construction": true});
            skPoint(sketch, "E4.6.4.5", {"position": v(196.76, -136.22) * mm});
            skLineSegment(sketch, "E4.6.5.0", {"start": v(181.62, -151.35) * mm, "end": v(181.62, -181.62) * mm, "construction": true});
            skLineSegment(sketch, "E4.6.5.1", {"start": v(196.76, -151.35) * mm, "end": v(196.76, -181.62) * mm, "construction": true});
            skLineSegment(sketch, "E4.6.5.2", {"start": v(211.89, -151.35) * mm, "end": v(211.89, -181.62) * mm, "construction": true});
            skLineSegment(sketch, "E4.6.5.3", {"start": v(181.62, -151.35) * mm, "end": v(211.89, -151.35) * mm, "construction": true});
            skLineSegment(sketch, "E4.6.5.4", {"start": v(181.62, -181.62) * mm, "end": v(211.89, -181.62) * mm, "construction": true});
            skPoint(sketch, "E4.6.5.5", {"position": v(196.76, -166.49) * mm});
            skLineSegment(sketch, "E4.6.6.0", {"start": v(181.62, -181.62) * mm, "end": v(181.62, -211.89) * mm, "construction": true});
            skLineSegment(sketch, "E4.6.6.1", {"start": v(196.76, -181.62) * mm, "end": v(196.76, -211.9) * mm, "construction": true});
            skLineSegment(sketch, "E4.6.6.2", {"start": v(211.89, -181.62) * mm, "end": v(211.89, -211.89) * mm, "construction": true});
            skLineSegment(sketch, "E4.6.6.3", {"start": v(181.62, -181.62) * mm, "end": v(211.89, -181.62) * mm, "construction": true});
            skLineSegment(sketch, "E4.6.6.4", {"start": v(181.62, -211.89) * mm, "end": v(211.89, -211.89) * mm, "construction": true});
            skPoint(sketch, "E4.6.6.5", {"position": v(196.76, -196.76) * mm});
            skLineSegment(sketch, "E4.6.7.0", {"start": v(181.62, -211.9) * mm, "end": v(181.62, -242.16) * mm, "construction": true});
            skLineSegment(sketch, "E4.6.7.1", {"start": v(196.76, -211.9) * mm, "end": v(196.76, -242.16) * mm, "construction": true});
            skLineSegment(sketch, "E4.6.7.2", {"start": v(211.89, -211.9) * mm, "end": v(211.89, -242.16) * mm, "construction": true});
            skLineSegment(sketch, "E4.6.7.3", {"start": v(181.62, -211.9) * mm, "end": v(211.89, -211.9) * mm, "construction": true});
            skLineSegment(sketch, "E4.6.7.4", {"start": v(181.62, -242.16) * mm, "end": v(211.89, -242.16) * mm, "construction": true});
            skPoint(sketch, "E4.6.7.5", {"position": v(196.76, -227.03) * mm});
            skLineSegment(sketch, "E4.6.8.0", {"start": v(181.62, -242.16) * mm, "end": v(181.62, -272.43) * mm, "construction": true});
            skLineSegment(sketch, "E4.6.8.1", {"start": v(196.76, -242.16) * mm, "end": v(196.76, -272.43) * mm, "construction": true});
            skLineSegment(sketch, "E4.6.8.2", {"start": v(211.89, -242.16) * mm, "end": v(211.89, -272.43) * mm, "construction": true});
            skLineSegment(sketch, "E4.6.8.3", {"start": v(181.62, -242.16) * mm, "end": v(211.89, -242.16) * mm, "construction": true});
            skLineSegment(sketch, "E4.6.8.4", {"start": v(181.62, -272.43) * mm, "end": v(211.89, -272.43) * mm, "construction": true});
            skPoint(sketch, "E4.6.8.5", {"position": v(196.76, -257.3) * mm});
            skLineSegment(sketch, "E4.7.0.0", {"start": v(211.9, 0) * mm, "end": v(211.9, -30.27) * mm, "construction": true});
            skLineSegment(sketch, "E4.7.0.1", {"start": v(227.03, 0) * mm, "end": v(227.03, -30.27) * mm, "construction": true});
            skLineSegment(sketch, "E4.7.0.2", {"start": v(242.16, 0) * mm, "end": v(242.16, -30.27) * mm, "construction": true});
            skLineSegment(sketch, "E4.7.0.3", {"start": v(211.9, 0) * mm, "end": v(242.16, 0) * mm, "construction": true});
            skLineSegment(sketch, "E4.7.0.4", {"start": v(211.9, -30.27) * mm, "end": v(242.16, -30.27) * mm, "construction": true});
            skPoint(sketch, "E4.7.0.5", {"position": v(227.03, -15.14) * mm});
            skLineSegment(sketch, "E4.7.1.0", {"start": v(211.9, -30.27) * mm, "end": v(211.9, -60.54) * mm, "construction": true});
            skLineSegment(sketch, "E4.7.1.1", {"start": v(227.03, -30.27) * mm, "end": v(227.03, -60.54) * mm, "construction": true});
            skLineSegment(sketch, "E4.7.1.2", {"start": v(242.16, -30.27) * mm, "end": v(242.16, -60.54) * mm, "construction": true});
            skLineSegment(sketch, "E4.7.1.3", {"start": v(211.9, -30.27) * mm, "end": v(242.16, -30.27) * mm, "construction": true});
            skLineSegment(sketch, "E4.7.1.4", {"start": v(211.9, -60.54) * mm, "end": v(242.16, -60.54) * mm, "construction": true});
            skPoint(sketch, "E4.7.1.5", {"position": v(227.03, -45.4) * mm});
            skLineSegment(sketch, "E4.7.2.0", {"start": v(211.9, -60.54) * mm, "end": v(211.9, -90.81) * mm, "construction": true});
            skLineSegment(sketch, "E4.7.2.1", {"start": v(227.03, -60.54) * mm, "end": v(227.03, -90.81) * mm, "construction": true});
            skLineSegment(sketch, "E4.7.2.2", {"start": v(242.16, -60.54) * mm, "end": v(242.16, -90.81) * mm, "construction": true});
            skLineSegment(sketch, "E4.7.2.3", {"start": v(211.9, -60.54) * mm, "end": v(242.16, -60.54) * mm, "construction": true});
            skLineSegment(sketch, "E4.7.2.4", {"start": v(211.9, -90.81) * mm, "end": v(242.16, -90.81) * mm, "construction": true});
            skPoint(sketch, "E4.7.2.5", {"position": v(227.03, -75.68) * mm});
            skLineSegment(sketch, "E4.7.3.0", {"start": v(211.9, -90.81) * mm, "end": v(211.9, -121.08) * mm, "construction": true});
            skLineSegment(sketch, "E4.7.3.1", {"start": v(227.03, -90.81) * mm, "end": v(227.03, -121.08) * mm, "construction": true});
            skLineSegment(sketch, "E4.7.3.2", {"start": v(242.16, -90.81) * mm, "end": v(242.16, -121.08) * mm, "construction": true});
            skLineSegment(sketch, "E4.7.3.3", {"start": v(211.9, -90.81) * mm, "end": v(242.16, -90.81) * mm, "construction": true});
            skLineSegment(sketch, "E4.7.3.4", {"start": v(211.9, -121.08) * mm, "end": v(242.16, -121.08) * mm, "construction": true});
            skPoint(sketch, "E4.7.3.5", {"position": v(227.03, -105.94) * mm});
            skLineSegment(sketch, "E4.7.4.0", {"start": v(211.9, -121.08) * mm, "end": v(211.9, -151.35) * mm, "construction": true});
            skLineSegment(sketch, "E4.7.4.1", {"start": v(227.03, -121.08) * mm, "end": v(227.03, -151.35) * mm, "construction": true});
            skLineSegment(sketch, "E4.7.4.2", {"start": v(242.16, -121.08) * mm, "end": v(242.16, -151.35) * mm, "construction": true});
            skLineSegment(sketch, "E4.7.4.3", {"start": v(211.9, -121.08) * mm, "end": v(242.16, -121.08) * mm, "construction": true});
            skLineSegment(sketch, "E4.7.4.4", {"start": v(211.9, -151.35) * mm, "end": v(242.16, -151.35) * mm, "construction": true});
            skPoint(sketch, "E4.7.4.5", {"position": v(227.03, -136.22) * mm});
            skLineSegment(sketch, "E4.7.5.0", {"start": v(211.9, -151.35) * mm, "end": v(211.9, -181.62) * mm, "construction": true});
            skLineSegment(sketch, "E4.7.5.1", {"start": v(227.03, -151.35) * mm, "end": v(227.03, -181.62) * mm, "construction": true});
            skLineSegment(sketch, "E4.7.5.2", {"start": v(242.16, -151.35) * mm, "end": v(242.16, -181.62) * mm, "construction": true});
            skLineSegment(sketch, "E4.7.5.3", {"start": v(211.9, -151.35) * mm, "end": v(242.16, -151.35) * mm, "construction": true});
            skLineSegment(sketch, "E4.7.5.4", {"start": v(211.9, -181.62) * mm, "end": v(242.16, -181.62) * mm, "construction": true});
            skPoint(sketch, "E4.7.5.5", {"position": v(227.03, -166.49) * mm});
            skLineSegment(sketch, "E4.7.6.0", {"start": v(211.9, -181.62) * mm, "end": v(211.9, -211.89) * mm, "construction": true});
            skLineSegment(sketch, "E4.7.6.1", {"start": v(227.03, -181.62) * mm, "end": v(227.03, -211.9) * mm, "construction": true});
            skLineSegment(sketch, "E4.7.6.2", {"start": v(242.16, -181.62) * mm, "end": v(242.16, -211.89) * mm, "construction": true});
            skLineSegment(sketch, "E4.7.6.3", {"start": v(211.9, -181.62) * mm, "end": v(242.16, -181.62) * mm, "construction": true});
            skLineSegment(sketch, "E4.7.6.4", {"start": v(211.9, -211.89) * mm, "end": v(242.16, -211.89) * mm, "construction": true});
            skPoint(sketch, "E4.7.6.5", {"position": v(227.03, -196.76) * mm});
            skLineSegment(sketch, "E4.7.7.0", {"start": v(211.9, -211.9) * mm, "end": v(211.9, -242.16) * mm, "construction": true});
            skLineSegment(sketch, "E4.7.7.1", {"start": v(227.03, -211.9) * mm, "end": v(227.03, -242.16) * mm, "construction": true});
            skLineSegment(sketch, "E4.7.7.2", {"start": v(242.16, -211.9) * mm, "end": v(242.16, -242.16) * mm, "construction": true});
            skLineSegment(sketch, "E4.7.7.3", {"start": v(211.9, -211.9) * mm, "end": v(242.16, -211.9) * mm, "construction": true});
            skLineSegment(sketch, "E4.7.7.4", {"start": v(211.9, -242.16) * mm, "end": v(242.16, -242.16) * mm, "construction": true});
            skPoint(sketch, "E4.7.7.5", {"position": v(227.03, -227.03) * mm});
            skLineSegment(sketch, "E4.7.8.0", {"start": v(211.9, -242.16) * mm, "end": v(211.9, -272.43) * mm, "construction": true});
            skLineSegment(sketch, "E4.7.8.1", {"start": v(227.03, -242.16) * mm, "end": v(227.03, -272.43) * mm, "construction": true});
            skLineSegment(sketch, "E4.7.8.2", {"start": v(242.16, -242.16) * mm, "end": v(242.16, -272.43) * mm, "construction": true});
            skLineSegment(sketch, "E4.7.8.3", {"start": v(211.9, -242.16) * mm, "end": v(242.16, -242.16) * mm, "construction": true});
            skLineSegment(sketch, "E4.7.8.4", {"start": v(211.9, -272.43) * mm, "end": v(242.16, -272.43) * mm, "construction": true});
            skPoint(sketch, "E4.7.8.5", {"position": v(227.03, -257.3) * mm});
            skLineSegment(sketch, "E4.8.0.0", {"start": v(242.16, 0) * mm, "end": v(242.16, -30.27) * mm, "construction": true});
            skLineSegment(sketch, "E4.8.0.1", {"start": v(257.3, 0) * mm, "end": v(257.3, -30.27) * mm, "construction": true});
            skLineSegment(sketch, "E4.8.0.2", {"start": v(272.43, 0) * mm, "end": v(272.43, -30.27) * mm, "construction": true});
            skLineSegment(sketch, "E4.8.0.3", {"start": v(242.16, 0) * mm, "end": v(272.43, 0) * mm, "construction": true});
            skLineSegment(sketch, "E4.8.0.4", {"start": v(242.16, -30.27) * mm, "end": v(272.43, -30.27) * mm, "construction": true});
            skPoint(sketch, "E4.8.0.5", {"position": v(257.3, -15.14) * mm});
            skLineSegment(sketch, "E4.8.1.0", {"start": v(242.16, -30.27) * mm, "end": v(242.16, -60.54) * mm, "construction": true});
            skLineSegment(sketch, "E4.8.1.1", {"start": v(257.3, -30.27) * mm, "end": v(257.3, -60.54) * mm, "construction": true});
            skLineSegment(sketch, "E4.8.1.2", {"start": v(272.43, -30.27) * mm, "end": v(272.43, -60.54) * mm, "construction": true});
            skLineSegment(sketch, "E4.8.1.3", {"start": v(242.16, -30.27) * mm, "end": v(272.43, -30.27) * mm, "construction": true});
            skLineSegment(sketch, "E4.8.1.4", {"start": v(242.16, -60.54) * mm, "end": v(272.43, -60.54) * mm, "construction": true});
            skPoint(sketch, "E4.8.1.5", {"position": v(257.3, -45.4) * mm});
            skLineSegment(sketch, "E4.8.2.0", {"start": v(242.16, -60.54) * mm, "end": v(242.16, -90.81) * mm, "construction": true});
            skLineSegment(sketch, "E4.8.2.1", {"start": v(257.3, -60.54) * mm, "end": v(257.3, -90.81) * mm, "construction": true});
            skLineSegment(sketch, "E4.8.2.2", {"start": v(272.43, -60.54) * mm, "end": v(272.43, -90.81) * mm, "construction": true});
            skLineSegment(sketch, "E4.8.2.3", {"start": v(242.16, -60.54) * mm, "end": v(272.43, -60.54) * mm, "construction": true});
            skLineSegment(sketch, "E4.8.2.4", {"start": v(242.16, -90.81) * mm, "end": v(272.43, -90.81) * mm, "construction": true});
            skPoint(sketch, "E4.8.2.5", {"position": v(257.3, -75.68) * mm});
            skLineSegment(sketch, "E4.8.3.0", {"start": v(242.16, -90.81) * mm, "end": v(242.16, -121.08) * mm, "construction": true});
            skLineSegment(sketch, "E4.8.3.1", {"start": v(257.3, -90.81) * mm, "end": v(257.3, -121.08) * mm, "construction": true});
            skLineSegment(sketch, "E4.8.3.2", {"start": v(272.43, -90.81) * mm, "end": v(272.43, -121.08) * mm, "construction": true});
            skLineSegment(sketch, "E4.8.3.3", {"start": v(242.16, -90.81) * mm, "end": v(272.43, -90.81) * mm, "construction": true});
            skLineSegment(sketch, "E4.8.3.4", {"start": v(242.16, -121.08) * mm, "end": v(272.43, -121.08) * mm, "construction": true});
            skPoint(sketch, "E4.8.3.5", {"position": v(257.3, -105.94) * mm});
            skLineSegment(sketch, "E4.8.4.0", {"start": v(242.16, -121.08) * mm, "end": v(242.16, -151.35) * mm, "construction": true});
            skLineSegment(sketch, "E4.8.4.1", {"start": v(257.3, -121.08) * mm, "end": v(257.3, -151.35) * mm, "construction": true});
            skLineSegment(sketch, "E4.8.4.2", {"start": v(272.43, -121.08) * mm, "end": v(272.43, -151.35) * mm, "construction": true});
            skLineSegment(sketch, "E4.8.4.3", {"start": v(242.16, -121.08) * mm, "end": v(272.43, -121.08) * mm, "construction": true});
            skLineSegment(sketch, "E4.8.4.4", {"start": v(242.16, -151.35) * mm, "end": v(272.43, -151.35) * mm, "construction": true});
            skPoint(sketch, "E4.8.4.5", {"position": v(257.3, -136.22) * mm});
            skLineSegment(sketch, "E4.8.5.0", {"start": v(242.16, -151.35) * mm, "end": v(242.16, -181.62) * mm, "construction": true});
            skLineSegment(sketch, "E4.8.5.1", {"start": v(257.3, -151.35) * mm, "end": v(257.3, -181.62) * mm, "construction": true});
            skLineSegment(sketch, "E4.8.5.2", {"start": v(272.43, -151.35) * mm, "end": v(272.43, -181.62) * mm, "construction": true});
            skLineSegment(sketch, "E4.8.5.3", {"start": v(242.16, -151.35) * mm, "end": v(272.43, -151.35) * mm, "construction": true});
            skLineSegment(sketch, "E4.8.5.4", {"start": v(242.16, -181.62) * mm, "end": v(272.43, -181.62) * mm, "construction": true});
            skPoint(sketch, "E4.8.5.5", {"position": v(257.3, -166.49) * mm});
            skLineSegment(sketch, "E4.8.6.0", {"start": v(242.16, -181.62) * mm, "end": v(242.16, -211.89) * mm, "construction": true});
            skLineSegment(sketch, "E4.8.6.1", {"start": v(257.3, -181.62) * mm, "end": v(257.3, -211.9) * mm, "construction": true});
            skLineSegment(sketch, "E4.8.6.2", {"start": v(272.43, -181.62) * mm, "end": v(272.43, -211.89) * mm, "construction": true});
            skLineSegment(sketch, "E4.8.6.3", {"start": v(242.16, -181.62) * mm, "end": v(272.43, -181.62) * mm, "construction": true});
            skLineSegment(sketch, "E4.8.6.4", {"start": v(242.16, -211.89) * mm, "end": v(272.43, -211.89) * mm, "construction": true});
            skPoint(sketch, "E4.8.6.5", {"position": v(257.3, -196.76) * mm});
            skLineSegment(sketch, "E4.8.7.0", {"start": v(242.16, -211.9) * mm, "end": v(242.16, -242.16) * mm, "construction": true});
            skLineSegment(sketch, "E4.8.7.1", {"start": v(257.3, -211.9) * mm, "end": v(257.3, -242.16) * mm, "construction": true});
            skLineSegment(sketch, "E4.8.7.2", {"start": v(272.43, -211.9) * mm, "end": v(272.43, -242.16) * mm, "construction": true});
            skLineSegment(sketch, "E4.8.7.3", {"start": v(242.16, -211.9) * mm, "end": v(272.43, -211.9) * mm, "construction": true});
            skLineSegment(sketch, "E4.8.7.4", {"start": v(242.16, -242.16) * mm, "end": v(272.43, -242.16) * mm, "construction": true});
            skPoint(sketch, "E4.8.7.5", {"position": v(257.3, -227.03) * mm});
            skLineSegment(sketch, "E4.8.8.0", {"start": v(242.16, -242.16) * mm, "end": v(242.16, -272.43) * mm, "construction": true});
            skLineSegment(sketch, "E4.8.8.1", {"start": v(257.3, -242.16) * mm, "end": v(257.3, -272.43) * mm, "construction": true});
            skLineSegment(sketch, "E4.8.8.2", {"start": v(272.43, -242.16) * mm, "end": v(272.43, -272.43) * mm, "construction": true});
            skLineSegment(sketch, "E4.8.8.3", {"start": v(242.16, -242.16) * mm, "end": v(272.43, -242.16) * mm, "construction": true});
            skLineSegment(sketch, "E4.8.8.4", {"start": v(242.16, -272.43) * mm, "end": v(272.43, -272.43) * mm, "construction": true});
            skPoint(sketch, "E4.8.8.5", {"position": v(257.3, -257.3) * mm});
            skLineSegment(sketch, "E4.direction2", {"start": v(0, -30.27) * mm, "end": v(0, -60.54) * mm, "construction": true});
            skSolve(sketch);
        }
        {
            var Q0;
            Q0=qCreatedBy(makeId("Top.planeOp"),FACE);
            var sketch = newSketch(context, id + "F1", { "sketchPlane" : qUnion([Q0])});
            skPoint(sketch, "E5.0", {"position": v(272.43, -272.43) * mm});
            skLineSegment(sketch, "E6.bottom", {"start": v(0, 0) * mm, "end": v(272.43, 0) * mm});
            skLineSegment(sketch, "E6.top", {"start": v(0, -272.43) * mm, "end": v(272.43, -272.43) * mm});
            skLineSegment(sketch, "E6.left", {"start": v(0, 0) * mm, "end": v(0, -272.43) * mm});
            skLineSegment(sketch, "E6.right", {"start": v(272.43, 0) * mm, "end": v(272.43, -272.43) * mm});
            skSolve(sketch);
        }
        {
            var Q0;
            Q0 = qSketchRegion(id + "F1", true);
            extrude(context, id + "F2", {"entities" : qUnion([Q0]), "oppositeDirection" : true, "depth" : 1 / 101.6 * mm, "offsetDistance" : 25 * mm});
        }
        {
            var Q0;
            Q0=sQuery(id+"F0.wireOp",VERTEX,"E4.1.0.5");
            var Q1;
            Q1=makeQuery(id+"F2.opExtrude","SWEPT_BODY",BODY,{"disambiguationData":[OSD([sQuery(id+"F1.wireOp",EDGE,"E6.bottom"),sQuery(id+"F1.wireOp",EDGE,"E6.top"),sQuery(id+"F1.wireOp",EDGE,"E6.left"),sQuery(id+"F1.wireOp",EDGE,"E6.right")])]});
            hole(context, id + "F3", {"style" : HoleStyle.SIMPLE, "endStyle" : HoleEndStyle.THROUGH, "holeDiameter" : 9.9 * mm, "majorDiameter" : 5 * mm, "isTappedThrough" : true, "tappedDepth" : 12 * mm, "tapClearance" : 3, "locations" : qUnion([Q0]), "scope" : qUnion([Q1])});
        }
        {
            var Q0;
            Q0=sQuery(id+"F0.wireOp",VERTEX,"E4.2.0.5");
            var Q1;
            Q1=makeQuery(id+"F2.opExtrude","SWEPT_BODY",BODY,{"disambiguationData":[OSD([sQuery(id+"F1.wireOp",EDGE,"E6.bottom"),sQuery(id+"F1.wireOp",EDGE,"E6.top"),sQuery(id+"F1.wireOp",EDGE,"E6.left"),sQuery(id+"F1.wireOp",EDGE,"E6.right")])]});
            hole(context, id + "F4", {"style" : HoleStyle.SIMPLE, "endStyle" : HoleEndStyle.THROUGH, "holeDiameter" : 10.72 * mm, "majorDiameter" : 5 * mm, "isTappedThrough" : true, "tappedDepth" : 12 * mm, "tapClearance" : 3, "locations" : qUnion([Q0]), "scope" : qUnion([Q1])});
        }
        {
            var Q0;
            Q0=sQuery(id+"F0.wireOp",VERTEX,"E4.3.0.5");
            var Q1;
            Q1=makeQuery(id+"F2.opExtrude","SWEPT_BODY",BODY,{"disambiguationData":[OSD([sQuery(id+"F1.wireOp",EDGE,"E6.bottom"),sQuery(id+"F1.wireOp",EDGE,"E6.top"),sQuery(id+"F1.wireOp",EDGE,"E6.left"),sQuery(id+"F1.wireOp",EDGE,"E6.right")])]});
            hole(context, id + "F5", {"style" : HoleStyle.SIMPLE, "endStyle" : HoleEndStyle.THROUGH, "holeDiameter" : 11.53 * mm, "majorDiameter" : 5 * mm, "isTappedThrough" : true, "tappedDepth" : 12 * mm, "tapClearance" : 3, "locations" : qUnion([Q0]), "scope" : qUnion([Q1])});
        }
        {
            var Q0;
            Q0=sQuery(id+"F0.wireOp",VERTEX,"E4.4.0.5");
            var Q1;
            Q1=makeQuery(id+"F2.opExtrude","SWEPT_BODY",BODY,{"disambiguationData":[OSD([sQuery(id+"F1.wireOp",EDGE,"E6.bottom"),sQuery(id+"F1.wireOp",EDGE,"E6.top"),sQuery(id+"F1.wireOp",EDGE,"E6.left"),sQuery(id+"F1.wireOp",EDGE,"E6.right")])]});
            hole(context, id + "F6", {"style" : HoleStyle.SIMPLE, "endStyle" : HoleEndStyle.THROUGH, "holeDiameter" : 11.95 * mm, "majorDiameter" : 5 * mm, "isTappedThrough" : true, "tappedDepth" : 12 * mm, "tapClearance" : 3, "locations" : qUnion([Q0]), "scope" : qUnion([Q1])});
        }
        {
            var Q0;
            Q0=sQuery(id+"F0.wireOp",VERTEX,"E4.5.0.5");
            var Q1;
            Q1=makeQuery(id+"F2.opExtrude","SWEPT_BODY",BODY,{"disambiguationData":[OSD([sQuery(id+"F1.wireOp",EDGE,"E6.bottom"),sQuery(id+"F1.wireOp",EDGE,"E6.top"),sQuery(id+"F1.wireOp",EDGE,"E6.left"),sQuery(id+"F1.wireOp",EDGE,"E6.right")])]});
            hole(context, id + "F7", {"style" : HoleStyle.SIMPLE, "endStyle" : HoleEndStyle.THROUGH, "holeDiameter" : 12.18 * mm, "majorDiameter" : 5 * mm, "isTappedThrough" : true, "tappedDepth" : 12 * mm, "tapClearance" : 3, "locations" : qUnion([Q0]), "scope" : qUnion([Q1])});
        }
        {
            var Q0;
            Q0=sQuery(id+"F0.wireOp",VERTEX,"E4.6.0.5");
            var Q1;
            Q1=makeQuery(id+"F2.opExtrude","SWEPT_BODY",BODY,{"disambiguationData":[OSD([sQuery(id+"F1.wireOp",EDGE,"E6.bottom"),sQuery(id+"F1.wireOp",EDGE,"E6.top"),sQuery(id+"F1.wireOp",EDGE,"E6.left"),sQuery(id+"F1.wireOp",EDGE,"E6.right")])]});
            hole(context, id + "F8", {"style" : HoleStyle.SIMPLE, "endStyle" : HoleEndStyle.THROUGH, "holeDiameter" : 12.37 * mm, "majorDiameter" : 5 * mm, "isTappedThrough" : true, "tappedDepth" : 12 * mm, "tapClearance" : 3, "locations" : qUnion([Q0]), "scope" : qUnion([Q1])});
        }
        {
            var Q0;
            Q0=sQuery(id+"F0.wireOp",VERTEX,"E4.7.0.5");
            var Q1;
            Q1=makeQuery(id+"F2.opExtrude","SWEPT_BODY",BODY,{"disambiguationData":[OSD([sQuery(id+"F1.wireOp",EDGE,"E6.bottom"),sQuery(id+"F1.wireOp",EDGE,"E6.top"),sQuery(id+"F1.wireOp",EDGE,"E6.left"),sQuery(id+"F1.wireOp",EDGE,"E6.right")])]});
            hole(context, id + "F9", {"style" : HoleStyle.SIMPLE, "endStyle" : HoleEndStyle.THROUGH, "holeDiameter" : 12.6 * mm, "majorDiameter" : 5 * mm, "isTappedThrough" : true, "tappedDepth" : 12 * mm, "tapClearance" : 3, "locations" : qUnion([Q0]), "scope" : qUnion([Q1])});
        }
        {
            var Q0;
            Q0=sQuery(id+"F0.wireOp",VERTEX,"E4.8.0.5");
            var Q1;
            Q1=makeQuery(id+"F2.opExtrude","SWEPT_BODY",BODY,{"disambiguationData":[OSD([sQuery(id+"F1.wireOp",EDGE,"E6.bottom"),sQuery(id+"F1.wireOp",EDGE,"E6.top"),sQuery(id+"F1.wireOp",EDGE,"E6.left"),sQuery(id+"F1.wireOp",EDGE,"E6.right")])]});
            hole(context, id + "F10", {"style" : HoleStyle.SIMPLE, "endStyle" : HoleEndStyle.THROUGH, "holeDiameter" : 12.78 * mm, "majorDiameter" : 5 * mm, "isTappedThrough" : true, "tappedDepth" : 12 * mm, "tapClearance" : 3, "locations" : qUnion([Q0]), "scope" : qUnion([Q1])});
        }
        {
            var Q0;
            Q0=sQuery(id+"F0.wireOp",VERTEX,"E4.0.1.5");
            var Q1;
            Q1=makeQuery(id+"F2.opExtrude","SWEPT_BODY",BODY,{"disambiguationData":[OSD([sQuery(id+"F1.wireOp",EDGE,"E6.bottom"),sQuery(id+"F1.wireOp",EDGE,"E6.top"),sQuery(id+"F1.wireOp",EDGE,"E6.left"),sQuery(id+"F1.wireOp",EDGE,"E6.right")])]});
            hole(context, id + "F11", {"style" : HoleStyle.SIMPLE, "endStyle" : HoleEndStyle.THROUGH, "holeDiameter" : 13 * mm, "majorDiameter" : 5 * mm, "isTappedThrough" : true, "tappedDepth" : 12 * mm, "tapClearance" : 3, "locations" : qUnion([Q0]), "scope" : qUnion([Q1])});
        }
        {
            var Q0;
            Q0=sQuery(id+"F0.wireOp",VERTEX,"E4.1.1.5");
            var Q1;
            Q1=makeQuery(id+"F2.opExtrude","SWEPT_BODY",BODY,{"disambiguationData":[OSD([sQuery(id+"F1.wireOp",EDGE,"E6.bottom"),sQuery(id+"F1.wireOp",EDGE,"E6.top"),sQuery(id+"F1.wireOp",EDGE,"E6.left"),sQuery(id+"F1.wireOp",EDGE,"E6.right")])]});
            hole(context, id + "F12", {"style" : HoleStyle.SIMPLE, "endStyle" : HoleEndStyle.THROUGH, "holeDiameter" : 13.21 * mm, "majorDiameter" : 5 * mm, "isTappedThrough" : true, "tappedDepth" : 12 * mm, "tapClearance" : 3, "locations" : qUnion([Q0]), "scope" : qUnion([Q1])});
        }
        {
            var Q0;
            Q0=sQuery(id+"F0.wireOp",VERTEX,"E4.2.1.5");
            var Q1;
            Q1=makeQuery(id+"F2.opExtrude","SWEPT_BODY",BODY,{"disambiguationData":[OSD([sQuery(id+"F1.wireOp",EDGE,"E6.bottom"),sQuery(id+"F1.wireOp",EDGE,"E6.top"),sQuery(id+"F1.wireOp",EDGE,"E6.left"),sQuery(id+"F1.wireOp",EDGE,"E6.right")])]});
            hole(context, id + "F13", {"style" : HoleStyle.SIMPLE, "endStyle" : HoleEndStyle.THROUGH, "holeDiameter" : 13.4 * mm, "majorDiameter" : 5 * mm, "isTappedThrough" : true, "tappedDepth" : 12 * mm, "tapClearance" : 3, "locations" : qUnion([Q0]), "scope" : qUnion([Q1])});
        }
        {
            var Q0;
            Q0=sQuery(id+"F0.wireOp",VERTEX,"E4.3.1.5");
            var Q1;
            Q1=makeQuery(id+"F2.opExtrude","SWEPT_BODY",BODY,{"disambiguationData":[OSD([sQuery(id+"F1.wireOp",EDGE,"E6.bottom"),sQuery(id+"F1.wireOp",EDGE,"E6.top"),sQuery(id+"F1.wireOp",EDGE,"E6.left"),sQuery(id+"F1.wireOp",EDGE,"E6.right")])]});
            hole(context, id + "F14", {"style" : HoleStyle.SIMPLE, "endStyle" : HoleEndStyle.THROUGH, "holeDiameter" : 13.6 * mm, "majorDiameter" : 5 * mm, "isTappedThrough" : true, "tappedDepth" : 12 * mm, "tapClearance" : 3, "locations" : qUnion([Q0]), "scope" : qUnion([Q1])});
        }
        {
            var Q0;
            Q0=sQuery(id+"F0.wireOp",VERTEX,"E4.4.1.5");
            var Q1;
            Q1=makeQuery(id+"F2.opExtrude","SWEPT_BODY",BODY,{"disambiguationData":[OSD([sQuery(id+"F1.wireOp",EDGE,"E6.bottom"),sQuery(id+"F1.wireOp",EDGE,"E6.top"),sQuery(id+"F1.wireOp",EDGE,"E6.left"),sQuery(id+"F1.wireOp",EDGE,"E6.right")])]});
            hole(context, id + "F15", {"style" : HoleStyle.SIMPLE, "endStyle" : HoleEndStyle.THROUGH, "holeDiameter" : 13.83 * mm, "majorDiameter" : 5 * mm, "isTappedThrough" : true, "tappedDepth" : 12 * mm, "tapClearance" : 3, "locations" : qUnion([Q0]), "scope" : qUnion([Q1])});
        }
        {
            var Q0;
            Q0=sQuery(id+"F0.wireOp",VERTEX,"E4.5.1.5");
            var Q1;
            Q1=makeQuery(id+"F2.opExtrude","SWEPT_BODY",BODY,{"disambiguationData":[OSD([sQuery(id+"F1.wireOp",EDGE,"E6.bottom"),sQuery(id+"F1.wireOp",EDGE,"E6.top"),sQuery(id+"F1.wireOp",EDGE,"E6.left"),sQuery(id+"F1.wireOp",EDGE,"E6.right")])]});
            hole(context, id + "F16", {"style" : HoleStyle.SIMPLE, "endStyle" : HoleEndStyle.THROUGH, "holeDiameter" : 14.05 * mm, "majorDiameter" : 5 * mm, "isTappedThrough" : true, "tappedDepth" : 12 * mm, "tapClearance" : 3, "locations" : qUnion([Q0]), "scope" : qUnion([Q1])});
        }
        {
            var Q0;
            Q0=sQuery(id+"F0.wireOp",VERTEX,"E4.6.1.5");
            var Q1;
            Q1=makeQuery(id+"F2.opExtrude","SWEPT_BODY",BODY,{"disambiguationData":[OSD([sQuery(id+"F1.wireOp",EDGE,"E6.bottom"),sQuery(id+"F1.wireOp",EDGE,"E6.top"),sQuery(id+"F1.wireOp",EDGE,"E6.left"),sQuery(id+"F1.wireOp",EDGE,"E6.right")])]});
            hole(context, id + "F17", {"style" : HoleStyle.SIMPLE, "endStyle" : HoleEndStyle.THROUGH, "holeDiameter" : 14.15 * mm, "majorDiameter" : 5 * mm, "isTappedThrough" : true, "tappedDepth" : 12 * mm, "tapClearance" : 3, "locations" : qUnion([Q0]), "scope" : qUnion([Q1])});
        }
        {
            var Q0;
            Q0=sQuery(id+"F0.wireOp",VERTEX,"E4.7.1.5");
            var Q1;
            Q1=makeQuery(id+"F2.opExtrude","SWEPT_BODY",BODY,{"disambiguationData":[OSD([sQuery(id+"F1.wireOp",EDGE,"E6.bottom"),sQuery(id+"F1.wireOp",EDGE,"E6.top"),sQuery(id+"F1.wireOp",EDGE,"E6.left"),sQuery(id+"F1.wireOp",EDGE,"E6.right")])]});
            hole(context, id + "F18", {"style" : HoleStyle.SIMPLE, "endStyle" : HoleEndStyle.THROUGH, "holeDiameter" : 14.25 * mm, "majorDiameter" : 5 * mm, "isTappedThrough" : true, "tappedDepth" : 12 * mm, "tapClearance" : 3, "locations" : qUnion([Q0]), "scope" : qUnion([Q1])});
        }
        {
            var Q0;
            Q0=sQuery(id+"F0.wireOp",VERTEX,"E4.8.1.5");
            var Q1;
            Q1=makeQuery(id+"F2.opExtrude","SWEPT_BODY",BODY,{"disambiguationData":[OSD([sQuery(id+"F1.wireOp",EDGE,"E6.bottom"),sQuery(id+"F1.wireOp",EDGE,"E6.top"),sQuery(id+"F1.wireOp",EDGE,"E6.left"),sQuery(id+"F1.wireOp",EDGE,"E6.right")])]});
            hole(context, id + "F19", {"style" : HoleStyle.SIMPLE, "endStyle" : HoleEndStyle.THROUGH, "holeDiameter" : 14.36 * mm, "majorDiameter" : 5 * mm, "isTappedThrough" : true, "tappedDepth" : 12 * mm, "tapClearance" : 3, "locations" : qUnion([Q0]), "scope" : qUnion([Q1])});
        }
        {
            var Q0;
            Q0=sQuery(id+"F0.wireOp",VERTEX,"E4.0.2.5");
            var Q1;
            Q1=makeQuery(id+"F2.opExtrude","SWEPT_BODY",BODY,{"disambiguationData":[OSD([sQuery(id+"F1.wireOp",EDGE,"E6.bottom"),sQuery(id+"F1.wireOp",EDGE,"E6.top"),sQuery(id+"F1.wireOp",EDGE,"E6.left"),sQuery(id+"F1.wireOp",EDGE,"E6.right")])]});
            hole(context, id + "F20", {"style" : HoleStyle.SIMPLE, "endStyle" : HoleEndStyle.THROUGH, "holeDiameter" : 14.45 * mm, "majorDiameter" : 5 * mm, "isTappedThrough" : true, "tappedDepth" : 12 * mm, "tapClearance" : 3, "locations" : qUnion([Q0]), "scope" : qUnion([Q1])});
        }
        {
            var Q0;
            Q0=sQuery(id+"F0.wireOp",VERTEX,"E4.1.2.5");
            var Q1;
            Q1=makeQuery(id+"F2.opExtrude","SWEPT_BODY",BODY,{"disambiguationData":[OSD([sQuery(id+"F1.wireOp",EDGE,"E6.bottom"),sQuery(id+"F1.wireOp",EDGE,"E6.top"),sQuery(id+"F1.wireOp",EDGE,"E6.left"),sQuery(id+"F1.wireOp",EDGE,"E6.right")])]});
            hole(context, id + "F21", {"style" : HoleStyle.SIMPLE, "endStyle" : HoleEndStyle.THROUGH, "holeDiameter" : 14.56 * mm, "majorDiameter" : 5 * mm, "isTappedThrough" : true, "tappedDepth" : 12 * mm, "tapClearance" : 3, "locations" : qUnion([Q0]), "scope" : qUnion([Q1])});
        }
        {
            var Q0;
            Q0=sQuery(id+"F0.wireOp",VERTEX,"E4.2.2.5");
            var Q1;
            Q1=makeQuery(id+"F2.opExtrude","SWEPT_BODY",BODY,{"disambiguationData":[OSD([sQuery(id+"F1.wireOp",EDGE,"E6.bottom"),sQuery(id+"F1.wireOp",EDGE,"E6.top"),sQuery(id+"F1.wireOp",EDGE,"E6.left"),sQuery(id+"F1.wireOp",EDGE,"E6.right")])]});
            hole(context, id + "F22", {"style" : HoleStyle.SIMPLE, "endStyle" : HoleEndStyle.THROUGH, "holeDiameter" : 14.65 * mm, "majorDiameter" : 5 * mm, "isTappedThrough" : true, "tappedDepth" : 12 * mm, "tapClearance" : 3, "locations" : qUnion([Q0]), "scope" : qUnion([Q1])});
        }
        {
            var Q0;
            Q0=sQuery(id+"F0.wireOp",VERTEX,"E4.3.2.5");
            var Q1;
            Q1=makeQuery(id+"F2.opExtrude","SWEPT_BODY",BODY,{"disambiguationData":[OSD([sQuery(id+"F1.wireOp",EDGE,"E6.bottom"),sQuery(id+"F1.wireOp",EDGE,"E6.top"),sQuery(id+"F1.wireOp",EDGE,"E6.left"),sQuery(id+"F1.wireOp",EDGE,"E6.right")])]});
            hole(context, id + "F23", {"style" : HoleStyle.SIMPLE, "endStyle" : HoleEndStyle.THROUGH, "holeDiameter" : 14.86 * mm, "majorDiameter" : 5 * mm, "isTappedThrough" : true, "tappedDepth" : 12 * mm, "tapClearance" : 3, "locations" : qUnion([Q0]), "scope" : qUnion([Q1])});
        }
        {
            var Q0;
            Q0=sQuery(id+"F0.wireOp",VERTEX,"E4.4.2.5");
            var Q1;
            Q1=makeQuery(id+"F2.opExtrude","SWEPT_BODY",BODY,{"disambiguationData":[OSD([sQuery(id+"F1.wireOp",EDGE,"E6.bottom"),sQuery(id+"F1.wireOp",EDGE,"E6.top"),sQuery(id+"F1.wireOp",EDGE,"E6.left"),sQuery(id+"F1.wireOp",EDGE,"E6.right")])]});
            hole(context, id + "F24", {"style" : HoleStyle.SIMPLE, "endStyle" : HoleEndStyle.THROUGH, "holeDiameter" : 15.04 * mm, "majorDiameter" : 5 * mm, "isTappedThrough" : true, "tappedDepth" : 12 * mm, "tapClearance" : 3, "locations" : qUnion([Q0]), "scope" : qUnion([Q1])});
        }
        {
            var Q0;
            Q0=sQuery(id+"F0.wireOp",VERTEX,"E4.5.2.5");
            var Q1;
            Q1=makeQuery(id+"F2.opExtrude","SWEPT_BODY",BODY,{"disambiguationData":[OSD([sQuery(id+"F1.wireOp",EDGE,"E6.bottom"),sQuery(id+"F1.wireOp",EDGE,"E6.top"),sQuery(id+"F1.wireOp",EDGE,"E6.left"),sQuery(id+"F1.wireOp",EDGE,"E6.right")])]});
            hole(context, id + "F25", {"style" : HoleStyle.SIMPLE, "endStyle" : HoleEndStyle.THROUGH, "holeDiameter" : 15.27 * mm, "majorDiameter" : 5 * mm, "isTappedThrough" : true, "tappedDepth" : 12 * mm, "tapClearance" : 3, "locations" : qUnion([Q0]), "scope" : qUnion([Q1])});
        }
        {
            var Q0;
            Q0=sQuery(id+"F0.wireOp",VERTEX,"E4.6.2.5");
            var Q1;
            Q1=makeQuery(id+"F2.opExtrude","SWEPT_BODY",BODY,{"disambiguationData":[OSD([sQuery(id+"F1.wireOp",EDGE,"E6.bottom"),sQuery(id+"F1.wireOp",EDGE,"E6.top"),sQuery(id+"F1.wireOp",EDGE,"E6.left"),sQuery(id+"F1.wireOp",EDGE,"E6.right")])]});
            hole(context, id + "F26", {"style" : HoleStyle.SIMPLE, "endStyle" : HoleEndStyle.THROUGH, "holeDiameter" : 15.4 * mm, "majorDiameter" : 5 * mm, "isTappedThrough" : true, "tappedDepth" : 12 * mm, "tapClearance" : 3, "locations" : qUnion([Q0]), "scope" : qUnion([Q1])});
        }
        {
            var Q0;
            Q0=sQuery(id+"F0.wireOp",VERTEX,"E4.7.2.5");
            var Q1;
            Q1=makeQuery(id+"F2.opExtrude","SWEPT_BODY",BODY,{"disambiguationData":[OSD([sQuery(id+"F1.wireOp",EDGE,"E6.bottom"),sQuery(id+"F1.wireOp",EDGE,"E6.top"),sQuery(id+"F1.wireOp",EDGE,"E6.left"),sQuery(id+"F1.wireOp",EDGE,"E6.right")])]});
            hole(context, id + "F27", {"style" : HoleStyle.SIMPLE, "endStyle" : HoleEndStyle.THROUGH, "holeDiameter" : 15.53 * mm, "majorDiameter" : 5 * mm, "isTappedThrough" : true, "tappedDepth" : 12 * mm, "tapClearance" : 3, "locations" : qUnion([Q0]), "scope" : qUnion([Q1])});
        }
        {
            var Q0;
            Q0=sQuery(id+"F0.wireOp",VERTEX,"E4.8.2.5");
            var Q1;
            Q1=makeQuery(id+"F2.opExtrude","SWEPT_BODY",BODY,{"disambiguationData":[OSD([sQuery(id+"F1.wireOp",EDGE,"E6.bottom"),sQuery(id+"F1.wireOp",EDGE,"E6.top"),sQuery(id+"F1.wireOp",EDGE,"E6.left"),sQuery(id+"F1.wireOp",EDGE,"E6.right")])]});
            hole(context, id + "F28", {"style" : HoleStyle.SIMPLE, "endStyle" : HoleEndStyle.THROUGH, "holeDiameter" : 15.7 * mm, "majorDiameter" : 5 * mm, "isTappedThrough" : true, "tappedDepth" : 12 * mm, "tapClearance" : 3, "locations" : qUnion([Q0]), "scope" : qUnion([Q1])});
        }
        {
            var Q0;
            Q0=sQuery(id+"F0.wireOp",VERTEX,"E4.0.3.5");
            var Q1;
            Q1=makeQuery(id+"F2.opExtrude","SWEPT_BODY",BODY,{"disambiguationData":[OSD([sQuery(id+"F1.wireOp",EDGE,"E6.bottom"),sQuery(id+"F1.wireOp",EDGE,"E6.top"),sQuery(id+"F1.wireOp",EDGE,"E6.left"),sQuery(id+"F1.wireOp",EDGE,"E6.right")])]});
            hole(context, id + "F29", {"style" : HoleStyle.SIMPLE, "endStyle" : HoleEndStyle.THROUGH, "holeDiameter" : 15.8 * mm, "majorDiameter" : 5 * mm, "isTappedThrough" : true, "tappedDepth" : 12 * mm, "tapClearance" : 3, "locations" : qUnion([Q0]), "scope" : qUnion([Q1])});
        }
        {
            var Q0;
            Q0=sQuery(id+"F0.wireOp",VERTEX,"E4.1.3.5");
            var Q1;
            Q1=makeQuery(id+"F2.opExtrude","SWEPT_BODY",BODY,{"disambiguationData":[OSD([sQuery(id+"F1.wireOp",EDGE,"E6.bottom"),sQuery(id+"F1.wireOp",EDGE,"E6.top"),sQuery(id+"F1.wireOp",EDGE,"E6.left"),sQuery(id+"F1.wireOp",EDGE,"E6.right")])]});
            hole(context, id + "F30", {"style" : HoleStyle.SIMPLE, "endStyle" : HoleEndStyle.THROUGH, "holeDiameter" : 15.9 * mm, "majorDiameter" : 5 * mm, "isTappedThrough" : true, "tappedDepth" : 12 * mm, "tapClearance" : 3, "locations" : qUnion([Q0]), "scope" : qUnion([Q1])});
        }
        {
            var Q0;
            Q0=sQuery(id+"F0.wireOp",VERTEX,"E4.2.3.5");
            var Q1;
            Q1=makeQuery(id+"F2.opExtrude","SWEPT_BODY",BODY,{"disambiguationData":[OSD([sQuery(id+"F1.wireOp",EDGE,"E6.bottom"),sQuery(id+"F1.wireOp",EDGE,"E6.top"),sQuery(id+"F1.wireOp",EDGE,"E6.left"),sQuery(id+"F1.wireOp",EDGE,"E6.right")])]});
            hole(context, id + "F31", {"style" : HoleStyle.SIMPLE, "endStyle" : HoleEndStyle.THROUGH, "holeDiameter" : 16 * mm, "majorDiameter" : 5 * mm, "isTappedThrough" : true, "tappedDepth" : 12 * mm, "tapClearance" : 3, "locations" : qUnion([Q0]), "scope" : qUnion([Q1])});
        }
        {
            var Q0;
            Q0=sQuery(id+"F0.wireOp",VERTEX,"E4.3.3.5");
            var Q1;
            Q1=makeQuery(id+"F2.opExtrude","SWEPT_BODY",BODY,{"disambiguationData":[OSD([sQuery(id+"F1.wireOp",EDGE,"E6.bottom"),sQuery(id+"F1.wireOp",EDGE,"E6.top"),sQuery(id+"F1.wireOp",EDGE,"E6.left"),sQuery(id+"F1.wireOp",EDGE,"E6.right")])]});
            hole(context, id + "F32", {"style" : HoleStyle.SIMPLE, "endStyle" : HoleEndStyle.THROUGH, "holeDiameter" : 16.1 * mm, "majorDiameter" : 5 * mm, "isTappedThrough" : true, "tappedDepth" : 12 * mm, "tapClearance" : 3, "locations" : qUnion([Q0]), "scope" : qUnion([Q1])});
        }
        {
            var Q0;
            Q0=sQuery(id+"F0.wireOp",VERTEX,"E4.4.3.5");
            var Q1;
            Q1=makeQuery(id+"F2.opExtrude","SWEPT_BODY",BODY,{"disambiguationData":[OSD([sQuery(id+"F1.wireOp",EDGE,"E6.bottom"),sQuery(id+"F1.wireOp",EDGE,"E6.top"),sQuery(id+"F1.wireOp",EDGE,"E6.left"),sQuery(id+"F1.wireOp",EDGE,"E6.right")])]});
            hole(context, id + "F33", {"style" : HoleStyle.SIMPLE, "endStyle" : HoleEndStyle.THROUGH, "holeDiameter" : 16.3 * mm, "majorDiameter" : 5 * mm, "isTappedThrough" : true, "tappedDepth" : 12 * mm, "tapClearance" : 3, "locations" : qUnion([Q0]), "scope" : qUnion([Q1])});
        }
        {
            var Q0;
            Q0=sQuery(id+"F0.wireOp",VERTEX,"E4.5.3.5");
            var Q1;
            Q1=makeQuery(id+"F2.opExtrude","SWEPT_BODY",BODY,{"disambiguationData":[OSD([sQuery(id+"F1.wireOp",EDGE,"E6.bottom"),sQuery(id+"F1.wireOp",EDGE,"E6.top"),sQuery(id+"F1.wireOp",EDGE,"E6.left"),sQuery(id+"F1.wireOp",EDGE,"E6.right")])]});
            hole(context, id + "F34", {"style" : HoleStyle.SIMPLE, "endStyle" : HoleEndStyle.THROUGH, "holeDiameter" : 16.41 * mm, "majorDiameter" : 5 * mm, "isTappedThrough" : true, "tappedDepth" : 12 * mm, "tapClearance" : 3, "locations" : qUnion([Q0]), "scope" : qUnion([Q1])});
        }
        {
            var Q0;
            Q0=sQuery(id+"F0.wireOp",VERTEX,"E4.6.3.5");
            var Q1;
            Q1=makeQuery(id+"F2.opExtrude","SWEPT_BODY",BODY,{"disambiguationData":[OSD([sQuery(id+"F1.wireOp",EDGE,"E6.bottom"),sQuery(id+"F1.wireOp",EDGE,"E6.top"),sQuery(id+"F1.wireOp",EDGE,"E6.left"),sQuery(id+"F1.wireOp",EDGE,"E6.right")])]});
            hole(context, id + "F35", {"style" : HoleStyle.SIMPLE, "endStyle" : HoleEndStyle.THROUGH, "holeDiameter" : 16.51 * mm, "majorDiameter" : 5 * mm, "isTappedThrough" : true, "tappedDepth" : 12 * mm, "tapClearance" : 3, "locations" : qUnion([Q0]), "scope" : qUnion([Q1])});
        }
        {
            var Q0;
            Q0=sQuery(id+"F0.wireOp",VERTEX,"E4.7.3.5");
            var Q1;
            Q1=makeQuery(id+"F2.opExtrude","SWEPT_BODY",BODY,{"disambiguationData":[OSD([sQuery(id+"F1.wireOp",EDGE,"E6.bottom"),sQuery(id+"F1.wireOp",EDGE,"E6.top"),sQuery(id+"F1.wireOp",EDGE,"E6.left"),sQuery(id+"F1.wireOp",EDGE,"E6.right")])]});
            hole(context, id + "F36", {"style" : HoleStyle.SIMPLE, "endStyle" : HoleEndStyle.THROUGH, "holeDiameter" : 16.71 * mm, "majorDiameter" : 5 * mm, "isTappedThrough" : true, "tappedDepth" : 12 * mm, "tapClearance" : 3, "locations" : qUnion([Q0]), "scope" : qUnion([Q1])});
        }
        {
            var Q0;
            Q0=sQuery(id+"F0.wireOp",VERTEX,"E4.8.3.5");
            var Q1;
            Q1=makeQuery(id+"F2.opExtrude","SWEPT_BODY",BODY,{"disambiguationData":[OSD([sQuery(id+"F1.wireOp",EDGE,"E6.bottom"),sQuery(id+"F1.wireOp",EDGE,"E6.top"),sQuery(id+"F1.wireOp",EDGE,"E6.left"),sQuery(id+"F1.wireOp",EDGE,"E6.right")])]});
            hole(context, id + "F37", {"style" : HoleStyle.SIMPLE, "endStyle" : HoleEndStyle.THROUGH, "holeDiameter" : 16.92 * mm, "majorDiameter" : 5 * mm, "isTappedThrough" : true, "tappedDepth" : 12 * mm, "tapClearance" : 3, "locations" : qUnion([Q0]), "scope" : qUnion([Q1])});
        }
        {
            var Q0;
            Q0=sQuery(id+"F0.wireOp",VERTEX,"E4.0.4.5");
            var Q1;
            Q1=makeQuery(id+"F2.opExtrude","SWEPT_BODY",BODY,{"disambiguationData":[OSD([sQuery(id+"F1.wireOp",EDGE,"E6.bottom"),sQuery(id+"F1.wireOp",EDGE,"E6.top"),sQuery(id+"F1.wireOp",EDGE,"E6.left"),sQuery(id+"F1.wireOp",EDGE,"E6.right")])]});
            hole(context, id + "F38", {"style" : HoleStyle.SIMPLE, "endStyle" : HoleEndStyle.THROUGH, "holeDiameter" : 17.13 * mm, "majorDiameter" : 5 * mm, "isTappedThrough" : true, "tappedDepth" : 12 * mm, "tapClearance" : 3, "locations" : qUnion([Q0]), "scope" : qUnion([Q1])});
        }
        {
            var Q0;
            Q0=sQuery(id+"F0.wireOp",VERTEX,"E4.1.4.5");
            var Q1;
            Q1=makeQuery(id+"F2.opExtrude","SWEPT_BODY",BODY,{"disambiguationData":[OSD([sQuery(id+"F1.wireOp",EDGE,"E6.bottom"),sQuery(id+"F1.wireOp",EDGE,"E6.top"),sQuery(id+"F1.wireOp",EDGE,"E6.left"),sQuery(id+"F1.wireOp",EDGE,"E6.right")])]});
            hole(context, id + "F39", {"style" : HoleStyle.SIMPLE, "endStyle" : HoleEndStyle.THROUGH, "holeDiameter" : 17.35 * mm, "majorDiameter" : 5 * mm, "isTappedThrough" : true, "tappedDepth" : 12 * mm, "tapClearance" : 3, "locations" : qUnion([Q0]), "scope" : qUnion([Q1])});
        }
        {
            var Q0;
            Q0=makeQuery(id+"F2.opExtrude","SWEPT_EDGE",EDGE,{"disambiguationData":[OSD([sQuery(id+"F1.wireOp",EDGE,"E6.bottom"),sQuery(id+"F1.wireOp",EDGE,"E6.left")])]});
            var Q1;
            Q1=makeQuery(id+"F2.opExtrude","SWEPT_EDGE",EDGE,{"disambiguationData":[OSD([sQuery(id+"F1.wireOp",EDGE,"E6.bottom"),sQuery(id+"F1.wireOp",EDGE,"E6.right")])]});
            var Q2;
            Q2=makeQuery(id+"F2.opExtrude","SWEPT_EDGE",EDGE,{"disambiguationData":[OSD([sQuery(id+"F1.wireOp",EDGE,"E6.top"),sQuery(id+"F1.wireOp",EDGE,"E6.right")])]});
            var Q3;
            Q3=makeQuery(id+"F2.opExtrude","SWEPT_EDGE",EDGE,{"disambiguationData":[OSD([sQuery(id+"F1.wireOp",EDGE,"E6.top"),sQuery(id+"F1.wireOp",EDGE,"E6.left")])]});
            fillet(context, id + "F40", {"entities" : qUnion([Q0, Q1, Q2, Q3]), "radius" : 8 * mm, "tangentPropagation" : true, "allowEdgeOverflow" : false});
        }
        {
            var Q0;
            Q0=sQuery(id+"F0.wireOp",VERTEX,"E4.2.4.5");
            var Q1;
            Q1=makeQuery(id+"F2.opExtrude","SWEPT_BODY",BODY,{"disambiguationData":[OSD([sQuery(id+"F1.wireOp",EDGE,"E6.bottom"),sQuery(id+"F1.wireOp",EDGE,"E6.top"),sQuery(id+"F1.wireOp",EDGE,"E6.left"),sQuery(id+"F1.wireOp",EDGE,"E6.right")])]});
            hole(context, id + "F41", {"style" : HoleStyle.SIMPLE, "endStyle" : HoleEndStyle.THROUGH, "holeDiameter" : 17.45 * mm, "majorDiameter" : 5 * mm, "isTappedThrough" : true, "tappedDepth" : 12 * mm, "tapClearance" : 3, "locations" : qUnion([Q0]), "scope" : qUnion([Q1])});
        }
        {
            var Q0;
            Q0=sQuery(id+"F0.wireOp",VERTEX,"E4.3.4.5");
            var Q1;
            Q1=makeQuery(id+"F2.opExtrude","SWEPT_BODY",BODY,{"disambiguationData":[OSD([sQuery(id+"F1.wireOp",EDGE,"E6.bottom"),sQuery(id+"F1.wireOp",EDGE,"E6.top"),sQuery(id+"F1.wireOp",EDGE,"E6.left"),sQuery(id+"F1.wireOp",EDGE,"E6.right")])]});
            hole(context, id + "F42", {"style" : HoleStyle.SIMPLE, "endStyle" : HoleEndStyle.THROUGH, "holeDiameter" : 17.75 * mm, "majorDiameter" : 5 * mm, "isTappedThrough" : true, "tappedDepth" : 12 * mm, "tapClearance" : 3, "locations" : qUnion([Q0]), "scope" : qUnion([Q1])});
        }
        {
            var Q0;
            Q0=sQuery(id+"F0.wireOp",VERTEX,"E4.4.4.5");
            var Q1;
            Q1=makeQuery(id+"F2.opExtrude","SWEPT_BODY",BODY,{"disambiguationData":[OSD([sQuery(id+"F1.wireOp",EDGE,"E6.bottom"),sQuery(id+"F1.wireOp",EDGE,"E6.top"),sQuery(id+"F1.wireOp",EDGE,"E6.left"),sQuery(id+"F1.wireOp",EDGE,"E6.right")])]});
            hole(context, id + "F43", {"style" : HoleStyle.SIMPLE, "endStyle" : HoleEndStyle.THROUGH, "holeDiameter" : 17.97 * mm, "majorDiameter" : 5 * mm, "isTappedThrough" : true, "tappedDepth" : 12 * mm, "tapClearance" : 3, "locations" : qUnion([Q0]), "scope" : qUnion([Q1])});
        }
        {
            var Q0;
            Q0=sQuery(id+"F0.wireOp",VERTEX,"E4.5.4.5");
            var Q1;
            Q1=makeQuery(id+"F2.opExtrude","SWEPT_BODY",BODY,{"disambiguationData":[OSD([sQuery(id+"F1.wireOp",EDGE,"E6.bottom"),sQuery(id+"F1.wireOp",EDGE,"E6.top"),sQuery(id+"F1.wireOp",EDGE,"E6.left"),sQuery(id+"F1.wireOp",EDGE,"E6.right")])]});
            hole(context, id + "F44", {"style" : HoleStyle.SIMPLE, "endStyle" : HoleEndStyle.THROUGH, "holeDiameter" : 18.2 * mm, "majorDiameter" : 5 * mm, "isTappedThrough" : true, "tappedDepth" : 12 * mm, "tapClearance" : 3, "locations" : qUnion([Q0]), "scope" : qUnion([Q1])});
        }
        {
            var Q0;
            Q0=sQuery(id+"F0.wireOp",VERTEX,"E4.6.4.5");
            var Q1;
            Q1=makeQuery(id+"F2.opExtrude","SWEPT_BODY",BODY,{"disambiguationData":[OSD([sQuery(id+"F1.wireOp",EDGE,"E6.bottom"),sQuery(id+"F1.wireOp",EDGE,"E6.top"),sQuery(id+"F1.wireOp",EDGE,"E6.left"),sQuery(id+"F1.wireOp",EDGE,"E6.right")])]});
            hole(context, id + "F45", {"style" : HoleStyle.SIMPLE, "endStyle" : HoleEndStyle.THROUGH, "holeDiameter" : 18.35 * mm, "majorDiameter" : 5 * mm, "isTappedThrough" : true, "tappedDepth" : 12 * mm, "tapClearance" : 3, "locations" : qUnion([Q0]), "scope" : qUnion([Q1])});
        }
        {
            var Q0;
            Q0=sQuery(id+"F0.wireOp",VERTEX,"E4.7.4.5");
            var Q1;
            Q1=makeQuery(id+"F2.opExtrude","SWEPT_BODY",BODY,{"disambiguationData":[OSD([sQuery(id+"F1.wireOp",EDGE,"E6.bottom"),sQuery(id+"F1.wireOp",EDGE,"E6.top"),sQuery(id+"F1.wireOp",EDGE,"E6.left"),sQuery(id+"F1.wireOp",EDGE,"E6.right")])]});
            hole(context, id + "F46", {"style" : HoleStyle.SIMPLE, "endStyle" : HoleEndStyle.THROUGH, "holeDiameter" : 18.53 * mm, "majorDiameter" : 5 * mm, "isTappedThrough" : true, "tappedDepth" : 12 * mm, "tapClearance" : 3, "locations" : qUnion([Q0]), "scope" : qUnion([Q1])});
        }
        {
            var Q0;
            Q0=sQuery(id+"F0.wireOp",VERTEX,"E4.8.4.5");
            var Q1;
            Q1=makeQuery(id+"F2.opExtrude","SWEPT_BODY",BODY,{"disambiguationData":[OSD([sQuery(id+"F1.wireOp",EDGE,"E6.bottom"),sQuery(id+"F1.wireOp",EDGE,"E6.top"),sQuery(id+"F1.wireOp",EDGE,"E6.left"),sQuery(id+"F1.wireOp",EDGE,"E6.right")])]});
            hole(context, id + "F47", {"style" : HoleStyle.SIMPLE, "endStyle" : HoleEndStyle.THROUGH, "holeDiameter" : 18.6 * mm, "majorDiameter" : 5 * mm, "isTappedThrough" : true, "tappedDepth" : 12 * mm, "tapClearance" : 3, "locations" : qUnion([Q0]), "scope" : qUnion([Q1])});
        }
        {
            var Q0;
            Q0=sQuery(id+"F0.wireOp",VERTEX,"E4.0.5.5");
            var Q1;
            Q1=makeQuery(id+"F2.opExtrude","SWEPT_BODY",BODY,{"disambiguationData":[OSD([sQuery(id+"F1.wireOp",EDGE,"E6.bottom"),sQuery(id+"F1.wireOp",EDGE,"E6.top"),sQuery(id+"F1.wireOp",EDGE,"E6.left"),sQuery(id+"F1.wireOp",EDGE,"E6.right")])]});
            hole(context, id + "F48", {"style" : HoleStyle.SIMPLE, "endStyle" : HoleEndStyle.THROUGH, "holeDiameter" : 18.7 * mm, "majorDiameter" : 5 * mm, "isTappedThrough" : true, "tappedDepth" : 12 * mm, "tapClearance" : 3, "locations" : qUnion([Q0]), "scope" : qUnion([Q1])});
        }
        {
            var Q0;
            Q0=sQuery(id+"F0.wireOp",VERTEX,"E4.1.5.5");
            var Q1;
            Q1=makeQuery(id+"F2.opExtrude","SWEPT_BODY",BODY,{"disambiguationData":[OSD([sQuery(id+"F1.wireOp",EDGE,"E6.bottom"),sQuery(id+"F1.wireOp",EDGE,"E6.top"),sQuery(id+"F1.wireOp",EDGE,"E6.left"),sQuery(id+"F1.wireOp",EDGE,"E6.right")])]});
            hole(context, id + "F49", {"style" : HoleStyle.SIMPLE, "endStyle" : HoleEndStyle.THROUGH, "holeDiameter" : 18.8 * mm, "majorDiameter" : 5 * mm, "isTappedThrough" : true, "tappedDepth" : 12 * mm, "tapClearance" : 3, "locations" : qUnion([Q0]), "scope" : qUnion([Q1])});
        }
        {
            var Q0;
            Q0=sQuery(id+"F0.wireOp",VERTEX,"E4.2.5.5");
            var Q1;
            Q1=makeQuery(id+"F2.opExtrude","SWEPT_BODY",BODY,{"disambiguationData":[OSD([sQuery(id+"F1.wireOp",EDGE,"E6.bottom"),sQuery(id+"F1.wireOp",EDGE,"E6.top"),sQuery(id+"F1.wireOp",EDGE,"E6.left"),sQuery(id+"F1.wireOp",EDGE,"E6.right")])]});
            hole(context, id + "F50", {"style" : HoleStyle.SIMPLE, "endStyle" : HoleEndStyle.THROUGH, "holeDiameter" : 18.9 * mm, "majorDiameter" : 5 * mm, "isTappedThrough" : true, "tappedDepth" : 12 * mm, "tapClearance" : 3, "locations" : qUnion([Q0]), "scope" : qUnion([Q1])});
        }
        {
            var Q0;
            Q0=sQuery(id+"F0.wireOp",VERTEX,"E4.3.5.5");
            var Q1;
            Q1=makeQuery(id+"F2.opExtrude","SWEPT_BODY",BODY,{"disambiguationData":[OSD([sQuery(id+"F1.wireOp",EDGE,"E6.bottom"),sQuery(id+"F1.wireOp",EDGE,"E6.top"),sQuery(id+"F1.wireOp",EDGE,"E6.left"),sQuery(id+"F1.wireOp",EDGE,"E6.right")])]});
            hole(context, id + "F51", {"style" : HoleStyle.SIMPLE, "endStyle" : HoleEndStyle.THROUGH, "holeDiameter" : 19.1 * mm, "majorDiameter" : 5 * mm, "isTappedThrough" : true, "tappedDepth" : 12 * mm, "tapClearance" : 3, "locations" : qUnion([Q0]), "scope" : qUnion([Q1])});
        }
        {
            var Q0;
            Q0=sQuery(id+"F0.wireOp",VERTEX,"E4.4.5.5");
            var Q1;
            Q1=makeQuery(id+"F2.opExtrude","SWEPT_BODY",BODY,{"disambiguationData":[OSD([sQuery(id+"F1.wireOp",EDGE,"E6.bottom"),sQuery(id+"F1.wireOp",EDGE,"E6.top"),sQuery(id+"F1.wireOp",EDGE,"E6.left"),sQuery(id+"F1.wireOp",EDGE,"E6.right")])]});
            hole(context, id + "F52", {"style" : HoleStyle.SIMPLE, "endStyle" : HoleEndStyle.THROUGH, "holeDiameter" : 19.22 * mm, "majorDiameter" : 5 * mm, "isTappedThrough" : true, "tappedDepth" : 12 * mm, "tapClearance" : 3, "locations" : qUnion([Q0]), "scope" : qUnion([Q1])});
        }
        {
            var Q0;
            Q0=sQuery(id+"F0.wireOp",VERTEX,"E4.5.5.5");
            var Q1;
            Q1=makeQuery(id+"F2.opExtrude","SWEPT_BODY",BODY,{"disambiguationData":[OSD([sQuery(id+"F1.wireOp",EDGE,"E6.bottom"),sQuery(id+"F1.wireOp",EDGE,"E6.top"),sQuery(id+"F1.wireOp",EDGE,"E6.left"),sQuery(id+"F1.wireOp",EDGE,"E6.right")])]});
            hole(context, id + "F53", {"style" : HoleStyle.SIMPLE, "endStyle" : HoleEndStyle.THROUGH, "holeDiameter" : 19.3 * mm, "majorDiameter" : 5 * mm, "isTappedThrough" : true, "tappedDepth" : 12 * mm, "tapClearance" : 3, "locations" : qUnion([Q0]), "scope" : qUnion([Q1])});
        }
        {
            var Q0;
            Q0=sQuery(id+"F0.wireOp",VERTEX,"E4.6.5.5");
            var Q1;
            Q1=makeQuery(id+"F2.opExtrude","SWEPT_BODY",BODY,{"disambiguationData":[OSD([sQuery(id+"F1.wireOp",EDGE,"E6.bottom"),sQuery(id+"F1.wireOp",EDGE,"E6.top"),sQuery(id+"F1.wireOp",EDGE,"E6.left"),sQuery(id+"F1.wireOp",EDGE,"E6.right")])]});
            hole(context, id + "F54", {"style" : HoleStyle.SIMPLE, "endStyle" : HoleEndStyle.THROUGH, "holeDiameter" : 19.41 * mm, "majorDiameter" : 5 * mm, "isTappedThrough" : true, "tappedDepth" : 12 * mm, "tapClearance" : 3, "locations" : qUnion([Q0]), "scope" : qUnion([Q1])});
        }
        {
            var Q0;
            Q0=sQuery(id+"F0.wireOp",VERTEX,"E4.7.5.5");
            var Q1;
            Q1=makeQuery(id+"F2.opExtrude","SWEPT_BODY",BODY,{"disambiguationData":[OSD([sQuery(id+"F1.wireOp",EDGE,"E6.bottom"),sQuery(id+"F1.wireOp",EDGE,"E6.top"),sQuery(id+"F1.wireOp",EDGE,"E6.left"),sQuery(id+"F1.wireOp",EDGE,"E6.right")])]});
            hole(context, id + "F55", {"style" : HoleStyle.SIMPLE, "endStyle" : HoleEndStyle.THROUGH, "holeDiameter" : 19.51 * mm, "majorDiameter" : 5 * mm, "isTappedThrough" : true, "tappedDepth" : 12 * mm, "tapClearance" : 3, "locations" : qUnion([Q0]), "scope" : qUnion([Q1])});
        }
        {
            var Q0;
            Q0=sQuery(id+"F0.wireOp",VERTEX,"E4.8.5.5");
            var Q1;
            Q1=makeQuery(id+"F2.opExtrude","SWEPT_BODY",BODY,{"disambiguationData":[OSD([sQuery(id+"F1.wireOp",EDGE,"E6.bottom"),sQuery(id+"F1.wireOp",EDGE,"E6.top"),sQuery(id+"F1.wireOp",EDGE,"E6.left"),sQuery(id+"F1.wireOp",EDGE,"E6.right")])]});
            hole(context, id + "F56", {"style" : HoleStyle.SIMPLE, "endStyle" : HoleEndStyle.THROUGH, "holeDiameter" : 19.62 * mm, "majorDiameter" : 5 * mm, "isTappedThrough" : true, "tappedDepth" : 12 * mm, "tapClearance" : 3, "locations" : qUnion([Q0]), "scope" : qUnion([Q1])});
        }
        {
            var Q0;
            Q0=sQuery(id+"F0.wireOp",VERTEX,"E4.0.6.5");
            var Q1;
            Q1=makeQuery(id+"F2.opExtrude","SWEPT_BODY",BODY,{"disambiguationData":[OSD([sQuery(id+"F1.wireOp",EDGE,"E6.bottom"),sQuery(id+"F1.wireOp",EDGE,"E6.top"),sQuery(id+"F1.wireOp",EDGE,"E6.left"),sQuery(id+"F1.wireOp",EDGE,"E6.right")])]});
            hole(context, id + "F57", {"style" : HoleStyle.SIMPLE, "endStyle" : HoleEndStyle.THROUGH, "holeDiameter" : 19.84 * mm, "majorDiameter" : 5 * mm, "isTappedThrough" : true, "tappedDepth" : 12 * mm, "tapClearance" : 3, "locations" : qUnion([Q0]), "scope" : qUnion([Q1])});
        }
        {
            var Q0;
            Q0=sQuery(id+"F0.wireOp",VERTEX,"E4.1.6.5");
            var Q1;
            Q1=makeQuery(id+"F2.opExtrude","SWEPT_BODY",BODY,{"disambiguationData":[OSD([sQuery(id+"F1.wireOp",EDGE,"E6.bottom"),sQuery(id+"F1.wireOp",EDGE,"E6.top"),sQuery(id+"F1.wireOp",EDGE,"E6.left"),sQuery(id+"F1.wireOp",EDGE,"E6.right")])]});
            hole(context, id + "F58", {"style" : HoleStyle.SIMPLE, "endStyle" : HoleEndStyle.THROUGH, "holeDiameter" : 20.02 * mm, "majorDiameter" : 5 * mm, "isTappedThrough" : true, "tappedDepth" : 12 * mm, "tapClearance" : 3, "locations" : qUnion([Q0]), "scope" : qUnion([Q1])});
        }
        {
            var Q0;
            Q0=sQuery(id+"F0.wireOp",VERTEX,"E4.2.6.5");
            var Q1;
            Q1=makeQuery(id+"F2.opExtrude","SWEPT_BODY",BODY,{"disambiguationData":[OSD([sQuery(id+"F1.wireOp",EDGE,"E6.bottom"),sQuery(id+"F1.wireOp",EDGE,"E6.top"),sQuery(id+"F1.wireOp",EDGE,"E6.left"),sQuery(id+"F1.wireOp",EDGE,"E6.right")])]});
            hole(context, id + "F59", {"style" : HoleStyle.SIMPLE, "endStyle" : HoleEndStyle.THROUGH, "holeDiameter" : 20.2 * mm, "majorDiameter" : 5 * mm, "isTappedThrough" : true, "tappedDepth" : 12 * mm, "tapClearance" : 3, "locations" : qUnion([Q0]), "scope" : qUnion([Q1])});
        }
        {
            var Q0;
            Q0=sQuery(id+"F0.wireOp",VERTEX,"E4.3.6.5");
            var Q1;
            Q1=makeQuery(id+"F2.opExtrude","SWEPT_BODY",BODY,{"disambiguationData":[OSD([sQuery(id+"F1.wireOp",EDGE,"E6.bottom"),sQuery(id+"F1.wireOp",EDGE,"E6.top"),sQuery(id+"F1.wireOp",EDGE,"E6.left"),sQuery(id+"F1.wireOp",EDGE,"E6.right")])]});
            hole(context, id + "F60", {"style" : HoleStyle.SIMPLE, "endStyle" : HoleEndStyle.THROUGH, "holeDiameter" : 20.32 * mm, "majorDiameter" : 5 * mm, "isTappedThrough" : true, "tappedDepth" : 12 * mm, "tapClearance" : 3, "locations" : qUnion([Q0]), "scope" : qUnion([Q1])});
        }
        {
            var Q0;
            Q0=sQuery(id+"F0.wireOp",VERTEX,"E4.4.6.5");
            var Q1;
            Q1=makeQuery(id+"F2.opExtrude","SWEPT_BODY",BODY,{"disambiguationData":[OSD([sQuery(id+"F1.wireOp",EDGE,"E6.bottom"),sQuery(id+"F1.wireOp",EDGE,"E6.top"),sQuery(id+"F1.wireOp",EDGE,"E6.left"),sQuery(id+"F1.wireOp",EDGE,"E6.right")])]});
            hole(context, id + "F61", {"style" : HoleStyle.SIMPLE, "endStyle" : HoleEndStyle.THROUGH, "holeDiameter" : 20.44 * mm, "majorDiameter" : 5 * mm, "isTappedThrough" : true, "tappedDepth" : 12 * mm, "tapClearance" : 3, "locations" : qUnion([Q0]), "scope" : qUnion([Q1])});
        }
        {
            var Q0;
            Q0=sQuery(id+"F0.wireOp",VERTEX,"E4.5.6.5");
            var Q1;
            Q1=makeQuery(id+"F2.opExtrude","SWEPT_BODY",BODY,{"disambiguationData":[OSD([sQuery(id+"F1.wireOp",EDGE,"E6.bottom"),sQuery(id+"F1.wireOp",EDGE,"E6.top"),sQuery(id+"F1.wireOp",EDGE,"E6.left"),sQuery(id+"F1.wireOp",EDGE,"E6.right")])]});
            hole(context, id + "F62", {"style" : HoleStyle.SIMPLE, "endStyle" : HoleEndStyle.THROUGH, "holeDiameter" : 20.68 * mm, "majorDiameter" : 5 * mm, "isTappedThrough" : true, "tappedDepth" : 12 * mm, "tapClearance" : 3, "locations" : qUnion([Q0]), "scope" : qUnion([Q1])});
        }
        {
            var Q0;
            Q0=sQuery(id+"F0.wireOp",VERTEX,"E4.6.6.5");
            var Q1;
            Q1=makeQuery(id+"F2.opExtrude","SWEPT_BODY",BODY,{"disambiguationData":[OSD([sQuery(id+"F1.wireOp",EDGE,"E6.bottom"),sQuery(id+"F1.wireOp",EDGE,"E6.top"),sQuery(id+"F1.wireOp",EDGE,"E6.left"),sQuery(id+"F1.wireOp",EDGE,"E6.right")])]});
            hole(context, id + "F63", {"style" : HoleStyle.SIMPLE, "endStyle" : HoleEndStyle.THROUGH, "holeDiameter" : 20.76 * mm, "majorDiameter" : 5 * mm, "isTappedThrough" : true, "tappedDepth" : 12 * mm, "tapClearance" : 3, "locations" : qUnion([Q0]), "scope" : qUnion([Q1])});
        }
        {
            var Q0;
            Q0=sQuery(id+"F0.wireOp",VERTEX,"E4.7.6.5");
            var Q1;
            Q1=makeQuery(id+"F2.opExtrude","SWEPT_BODY",BODY,{"disambiguationData":[OSD([sQuery(id+"F1.wireOp",EDGE,"E6.bottom"),sQuery(id+"F1.wireOp",EDGE,"E6.top"),sQuery(id+"F1.wireOp",EDGE,"E6.left"),sQuery(id+"F1.wireOp",EDGE,"E6.right")])]});
            hole(context, id + "F64", {"style" : HoleStyle.SIMPLE, "endStyle" : HoleEndStyle.THROUGH, "holeDiameter" : 20.85 * mm, "majorDiameter" : 5 * mm, "isTappedThrough" : true, "tappedDepth" : 12 * mm, "tapClearance" : 3, "locations" : qUnion([Q0]), "scope" : qUnion([Q1])});
        }
        {
            var Q0;
            Q0=sQuery(id+"F0.wireOp",VERTEX,"E4.8.6.5");
            var Q1;
            Q1=makeQuery(id+"F2.opExtrude","SWEPT_BODY",BODY,{"disambiguationData":[OSD([sQuery(id+"F1.wireOp",EDGE,"E6.bottom"),sQuery(id+"F1.wireOp",EDGE,"E6.top"),sQuery(id+"F1.wireOp",EDGE,"E6.left"),sQuery(id+"F1.wireOp",EDGE,"E6.right")])]});
            hole(context, id + "F65", {"style" : HoleStyle.SIMPLE, "endStyle" : HoleEndStyle.THROUGH, "holeDiameter" : 20.94 * mm, "majorDiameter" : 5 * mm, "isTappedThrough" : true, "tappedDepth" : 12 * mm, "tapClearance" : 3, "locations" : qUnion([Q0]), "scope" : qUnion([Q1])});
        }
        {
            var Q0;
            Q0=sQuery(id+"F0.wireOp",VERTEX,"E4.0.7.5");
            var Q1;
            Q1=makeQuery(id+"F2.opExtrude","SWEPT_BODY",BODY,{"disambiguationData":[OSD([sQuery(id+"F1.wireOp",EDGE,"E6.bottom"),sQuery(id+"F1.wireOp",EDGE,"E6.top"),sQuery(id+"F1.wireOp",EDGE,"E6.left"),sQuery(id+"F1.wireOp",EDGE,"E6.right")])]});
            hole(context, id + "F66", {"style" : HoleStyle.SIMPLE, "endStyle" : HoleEndStyle.THROUGH, "holeDiameter" : 21.08 * mm, "majorDiameter" : 5 * mm, "isTappedThrough" : true, "tappedDepth" : 12 * mm, "tapClearance" : 3, "locations" : qUnion([Q0]), "scope" : qUnion([Q1])});
        }
        {
            var Q0;
            Q0=sQuery(id+"F0.wireOp",VERTEX,"E4.1.7.5");
            var Q1;
            Q1=makeQuery(id+"F2.opExtrude","SWEPT_BODY",BODY,{"disambiguationData":[OSD([sQuery(id+"F1.wireOp",EDGE,"E6.bottom"),sQuery(id+"F1.wireOp",EDGE,"E6.top"),sQuery(id+"F1.wireOp",EDGE,"E6.left"),sQuery(id+"F1.wireOp",EDGE,"E6.right")])]});
            hole(context, id + "F67", {"style" : HoleStyle.SIMPLE, "endStyle" : HoleEndStyle.THROUGH, "holeDiameter" : 21.18 * mm, "majorDiameter" : 5 * mm, "isTappedThrough" : true, "tappedDepth" : 12 * mm, "tapClearance" : 3, "locations" : qUnion([Q0]), "scope" : qUnion([Q1])});
        }
        {
            var Q0;
            Q0=sQuery(id+"F0.wireOp",VERTEX,"E4.2.7.5");
            var Q1;
            Q1=makeQuery(id+"F2.opExtrude","SWEPT_BODY",BODY,{"disambiguationData":[OSD([sQuery(id+"F1.wireOp",EDGE,"E6.bottom"),sQuery(id+"F1.wireOp",EDGE,"E6.top"),sQuery(id+"F1.wireOp",EDGE,"E6.left"),sQuery(id+"F1.wireOp",EDGE,"E6.right")])]});
            hole(context, id + "F68", {"style" : HoleStyle.SIMPLE, "endStyle" : HoleEndStyle.THROUGH, "holeDiameter" : 21.24 * mm, "majorDiameter" : 5 * mm, "isTappedThrough" : true, "tappedDepth" : 12 * mm, "tapClearance" : 3, "locations" : qUnion([Q0]), "scope" : qUnion([Q1])});
        }
        {
            var Q0;
            Q0=sQuery(id+"F0.wireOp",VERTEX,"E4.3.7.5");
            var Q1;
            Q1=makeQuery(id+"F2.opExtrude","SWEPT_BODY",BODY,{"disambiguationData":[OSD([sQuery(id+"F1.wireOp",EDGE,"E6.bottom"),sQuery(id+"F1.wireOp",EDGE,"E6.top"),sQuery(id+"F1.wireOp",EDGE,"E6.left"),sQuery(id+"F1.wireOp",EDGE,"E6.right")])]});
            hole(context, id + "F69", {"style" : HoleStyle.SIMPLE, "endStyle" : HoleEndStyle.THROUGH, "holeDiameter" : 21.3 * mm, "majorDiameter" : 5 * mm, "isTappedThrough" : true, "tappedDepth" : 12 * mm, "tapClearance" : 3, "locations" : qUnion([Q0]), "scope" : qUnion([Q1])});
        }
        {
            var Q0;
            Q0=sQuery(id+"F0.wireOp",VERTEX,"E4.4.7.5");
            var Q1;
            Q1=makeQuery(id+"F2.opExtrude","SWEPT_BODY",BODY,{"disambiguationData":[OSD([sQuery(id+"F1.wireOp",EDGE,"E6.bottom"),sQuery(id+"F1.wireOp",EDGE,"E6.top"),sQuery(id+"F1.wireOp",EDGE,"E6.left"),sQuery(id+"F1.wireOp",EDGE,"E6.right")])]});
            hole(context, id + "F70", {"style" : HoleStyle.SIMPLE, "endStyle" : HoleEndStyle.THROUGH, "holeDiameter" : 21.49 * mm, "majorDiameter" : 5 * mm, "isTappedThrough" : true, "tappedDepth" : 12 * mm, "tapClearance" : 3, "locations" : qUnion([Q0]), "scope" : qUnion([Q1])});
        }
        {
            var Q0;
            Q0=sQuery(id+"F0.wireOp",VERTEX,"E4.5.7.5");
            var Q1;
            Q1=makeQuery(id+"F2.opExtrude","SWEPT_BODY",BODY,{"disambiguationData":[OSD([sQuery(id+"F1.wireOp",EDGE,"E6.bottom"),sQuery(id+"F1.wireOp",EDGE,"E6.top"),sQuery(id+"F1.wireOp",EDGE,"E6.left"),sQuery(id+"F1.wireOp",EDGE,"E6.right")])]});
            hole(context, id + "F71", {"style" : HoleStyle.SIMPLE, "endStyle" : HoleEndStyle.THROUGH, "holeDiameter" : 21.7 * mm, "majorDiameter" : 5 * mm, "isTappedThrough" : true, "tappedDepth" : 12 * mm, "tapClearance" : 3, "locations" : qUnion([Q0]), "scope" : qUnion([Q1])});
        }
        {
            var Q0;
            Q0=sQuery(id+"F0.wireOp",VERTEX,"E4.6.7.5");
            var Q1;
            Q1=makeQuery(id+"F2.opExtrude","SWEPT_BODY",BODY,{"disambiguationData":[OSD([sQuery(id+"F1.wireOp",EDGE,"E6.bottom"),sQuery(id+"F1.wireOp",EDGE,"E6.top"),sQuery(id+"F1.wireOp",EDGE,"E6.left"),sQuery(id+"F1.wireOp",EDGE,"E6.right")])]});
            hole(context, id + "F72", {"style" : HoleStyle.SIMPLE, "endStyle" : HoleEndStyle.THROUGH, "holeDiameter" : 21.9 * mm, "majorDiameter" : 5 * mm, "isTappedThrough" : true, "tappedDepth" : 12 * mm, "tapClearance" : 3, "locations" : qUnion([Q0]), "scope" : qUnion([Q1])});
        }
        {
            var Q0;
            Q0=sQuery(id+"F0.wireOp",VERTEX,"E4.7.7.5");
            var Q1;
            Q1=makeQuery(id+"F2.opExtrude","SWEPT_BODY",BODY,{"disambiguationData":[OSD([sQuery(id+"F1.wireOp",EDGE,"E6.bottom"),sQuery(id+"F1.wireOp",EDGE,"E6.top"),sQuery(id+"F1.wireOp",EDGE,"E6.left"),sQuery(id+"F1.wireOp",EDGE,"E6.right")])]});
            hole(context, id + "F73", {"style" : HoleStyle.SIMPLE, "endStyle" : HoleEndStyle.THROUGH, "holeDiameter" : 22.1 * mm, "majorDiameter" : 5 * mm, "isTappedThrough" : true, "tappedDepth" : 12 * mm, "tapClearance" : 3, "locations" : qUnion([Q0]), "scope" : qUnion([Q1])});
        }
        {
            var Q0;
            Q0=sQuery(id+"F0.wireOp",VERTEX,"E4.8.7.5");
            var Q1;
            Q1=makeQuery(id+"F2.opExtrude","SWEPT_BODY",BODY,{"disambiguationData":[OSD([sQuery(id+"F1.wireOp",EDGE,"E6.bottom"),sQuery(id+"F1.wireOp",EDGE,"E6.top"),sQuery(id+"F1.wireOp",EDGE,"E6.left"),sQuery(id+"F1.wireOp",EDGE,"E6.right")])]});
            hole(context, id + "F74", {"style" : HoleStyle.SIMPLE, "endStyle" : HoleEndStyle.THROUGH, "holeDiameter" : 22.33 * mm, "majorDiameter" : 5 * mm, "isTappedThrough" : true, "tappedDepth" : 12 * mm, "tapClearance" : 3, "locations" : qUnion([Q0]), "scope" : qUnion([Q1])});
        }
        {
            var Q0;
            Q0=sQuery(id+"F0.wireOp",VERTEX,"E4.0.8.5");
            var Q1;
            Q1=makeQuery(id+"F2.opExtrude","SWEPT_BODY",BODY,{"disambiguationData":[OSD([sQuery(id+"F1.wireOp",EDGE,"E6.bottom"),sQuery(id+"F1.wireOp",EDGE,"E6.top"),sQuery(id+"F1.wireOp",EDGE,"E6.left"),sQuery(id+"F1.wireOp",EDGE,"E6.right")])]});
            hole(context, id + "F75", {"style" : HoleStyle.SIMPLE, "endStyle" : HoleEndStyle.THROUGH, "holeDiameter" : 22.6 * mm, "majorDiameter" : 5 * mm, "isTappedThrough" : true, "tappedDepth" : 12 * mm, "tapClearance" : 3, "locations" : qUnion([Q0]), "scope" : qUnion([Q1])});
        }
        {
            var Q0;
            Q0=sQuery(id+"F0.wireOp",VERTEX,"E4.1.8.5");
            var Q1;
            Q1=makeQuery(id+"F2.opExtrude","SWEPT_BODY",BODY,{"disambiguationData":[OSD([sQuery(id+"F1.wireOp",EDGE,"E6.bottom"),sQuery(id+"F1.wireOp",EDGE,"E6.top"),sQuery(id+"F1.wireOp",EDGE,"E6.left"),sQuery(id+"F1.wireOp",EDGE,"E6.right")])]});
            hole(context, id + "F76", {"style" : HoleStyle.SIMPLE, "endStyle" : HoleEndStyle.THROUGH, "holeDiameter" : 22.7 * mm, "majorDiameter" : 5 * mm, "isTappedThrough" : true, "tappedDepth" : 12 * mm, "tapClearance" : 3, "locations" : qUnion([Q0]), "scope" : qUnion([Q1])});
        }
        {
            var Q0;
            Q0=sQuery(id+"F0.wireOp",VERTEX,"E4.2.8.5");
            var Q1;
            Q1=makeQuery(id+"F2.opExtrude","SWEPT_BODY",BODY,{"disambiguationData":[OSD([sQuery(id+"F1.wireOp",EDGE,"E6.bottom"),sQuery(id+"F1.wireOp",EDGE,"E6.top"),sQuery(id+"F1.wireOp",EDGE,"E6.left"),sQuery(id+"F1.wireOp",EDGE,"E6.right")])]});
            hole(context, id + "F77", {"style" : HoleStyle.SIMPLE, "endStyle" : HoleEndStyle.THROUGH, "holeDiameter" : 22.92 * mm, "majorDiameter" : 5 * mm, "isTappedThrough" : true, "tappedDepth" : 12 * mm, "tapClearance" : 3, "locations" : qUnion([Q0]), "scope" : qUnion([Q1])});
        }
        {
            var Q0;
            Q0=sQuery(id+"F0.wireOp",VERTEX,"E4.3.8.5");
            var Q1;
            Q1=makeQuery(id+"F2.opExtrude","SWEPT_BODY",BODY,{"disambiguationData":[OSD([sQuery(id+"F1.wireOp",EDGE,"E6.bottom"),sQuery(id+"F1.wireOp",EDGE,"E6.top"),sQuery(id+"F1.wireOp",EDGE,"E6.left"),sQuery(id+"F1.wireOp",EDGE,"E6.right")])]});
            hole(context, id + "F78", {"style" : HoleStyle.SIMPLE, "endStyle" : HoleEndStyle.THROUGH, "holeDiameter" : 23.06 * mm, "majorDiameter" : 5 * mm, "isTappedThrough" : true, "tappedDepth" : 12 * mm, "tapClearance" : 3, "locations" : qUnion([Q0]), "scope" : qUnion([Q1])});
        }
        {
            var Q0;
            Q0=sQuery(id+"F0.wireOp",VERTEX,"E4.4.8.5");
            var Q1;
            Q1=makeQuery(id+"F2.opExtrude","SWEPT_BODY",BODY,{"disambiguationData":[OSD([sQuery(id+"F1.wireOp",EDGE,"E6.bottom"),sQuery(id+"F1.wireOp",EDGE,"E6.top"),sQuery(id+"F1.wireOp",EDGE,"E6.left"),sQuery(id+"F1.wireOp",EDGE,"E6.right")])]});
            hole(context, id + "F79", {"style" : HoleStyle.SIMPLE, "endStyle" : HoleEndStyle.THROUGH, "holeDiameter" : 23.24 * mm, "majorDiameter" : 5 * mm, "isTappedThrough" : true, "tappedDepth" : 12 * mm, "tapClearance" : 3, "locations" : qUnion([Q0]), "scope" : qUnion([Q1])});
        }
        {
            var Q0;
            Q0=sQuery(id+"F0.wireOp",VERTEX,"E4.5.8.5");
            var Q1;
            Q1=makeQuery(id+"F2.opExtrude","SWEPT_BODY",BODY,{"disambiguationData":[OSD([sQuery(id+"F1.wireOp",EDGE,"E6.bottom"),sQuery(id+"F1.wireOp",EDGE,"E6.top"),sQuery(id+"F1.wireOp",EDGE,"E6.left"),sQuery(id+"F1.wireOp",EDGE,"E6.right")])]});
            hole(context, id + "F80", {"style" : HoleStyle.SIMPLE, "endStyle" : HoleEndStyle.THROUGH, "holeDiameter" : 23.47 * mm, "majorDiameter" : 5 * mm, "isTappedThrough" : true, "tappedDepth" : 12 * mm, "tapClearance" : 3, "locations" : qUnion([Q0]), "scope" : qUnion([Q1])});
        }
        {
            var Q0;
            Q0=sQuery(id+"F0.wireOp",VERTEX,"E4.6.8.5");
            var Q1;
            Q1=makeQuery(id+"F2.opExtrude","SWEPT_BODY",BODY,{"disambiguationData":[OSD([sQuery(id+"F1.wireOp",EDGE,"E6.bottom"),sQuery(id+"F1.wireOp",EDGE,"E6.top"),sQuery(id+"F1.wireOp",EDGE,"E6.left"),sQuery(id+"F1.wireOp",EDGE,"E6.right")])]});
            hole(context, id + "F81", {"style" : HoleStyle.SIMPLE, "endStyle" : HoleEndStyle.THROUGH, "holeDiameter" : 23.55 * mm, "majorDiameter" : 5 * mm, "isTappedThrough" : true, "tappedDepth" : 12 * mm, "tapClearance" : 3, "locations" : qUnion([Q0]), "scope" : qUnion([Q1])});
        }
        {
            var Q0;
            Q0=sQuery(id+"F0.wireOp",VERTEX,"E4.7.8.5");
            var Q1;
            Q1=makeQuery(id+"F2.opExtrude","SWEPT_BODY",BODY,{"disambiguationData":[OSD([sQuery(id+"F1.wireOp",EDGE,"E6.bottom"),sQuery(id+"F1.wireOp",EDGE,"E6.top"),sQuery(id+"F1.wireOp",EDGE,"E6.left"),sQuery(id+"F1.wireOp",EDGE,"E6.right")])]});
            hole(context, id + "F82", {"style" : HoleStyle.SIMPLE, "endStyle" : HoleEndStyle.THROUGH, "holeDiameter" : 23.87 * mm, "majorDiameter" : 5 * mm, "isTappedThrough" : true, "tappedDepth" : 12 * mm, "tapClearance" : 3, "locations" : qUnion([Q0]), "scope" : qUnion([Q1])});
        }
        {
            var Q0;
            Q0=sQuery(id+"F0.wireOp",VERTEX,"E4.8.8.5");
            var Q1;
            Q1=makeQuery(id+"F2.opExtrude","SWEPT_BODY",BODY,{"disambiguationData":[OSD([sQuery(id+"F1.wireOp",EDGE,"E6.bottom"),sQuery(id+"F1.wireOp",EDGE,"E6.top"),sQuery(id+"F1.wireOp",EDGE,"E6.left"),sQuery(id+"F1.wireOp",EDGE,"E6.right")])]});
            hole(context, id + "F83", {"style" : HoleStyle.SIMPLE, "endStyle" : HoleEndStyle.THROUGH, "holeDiameter" : 24.27 * mm, "majorDiameter" : 5 * mm, "isTappedThrough" : true, "tappedDepth" : 12 * mm, "tapClearance" : 3, "locations" : qUnion([Q0]), "scope" : qUnion([Q1])});
        }
    });
